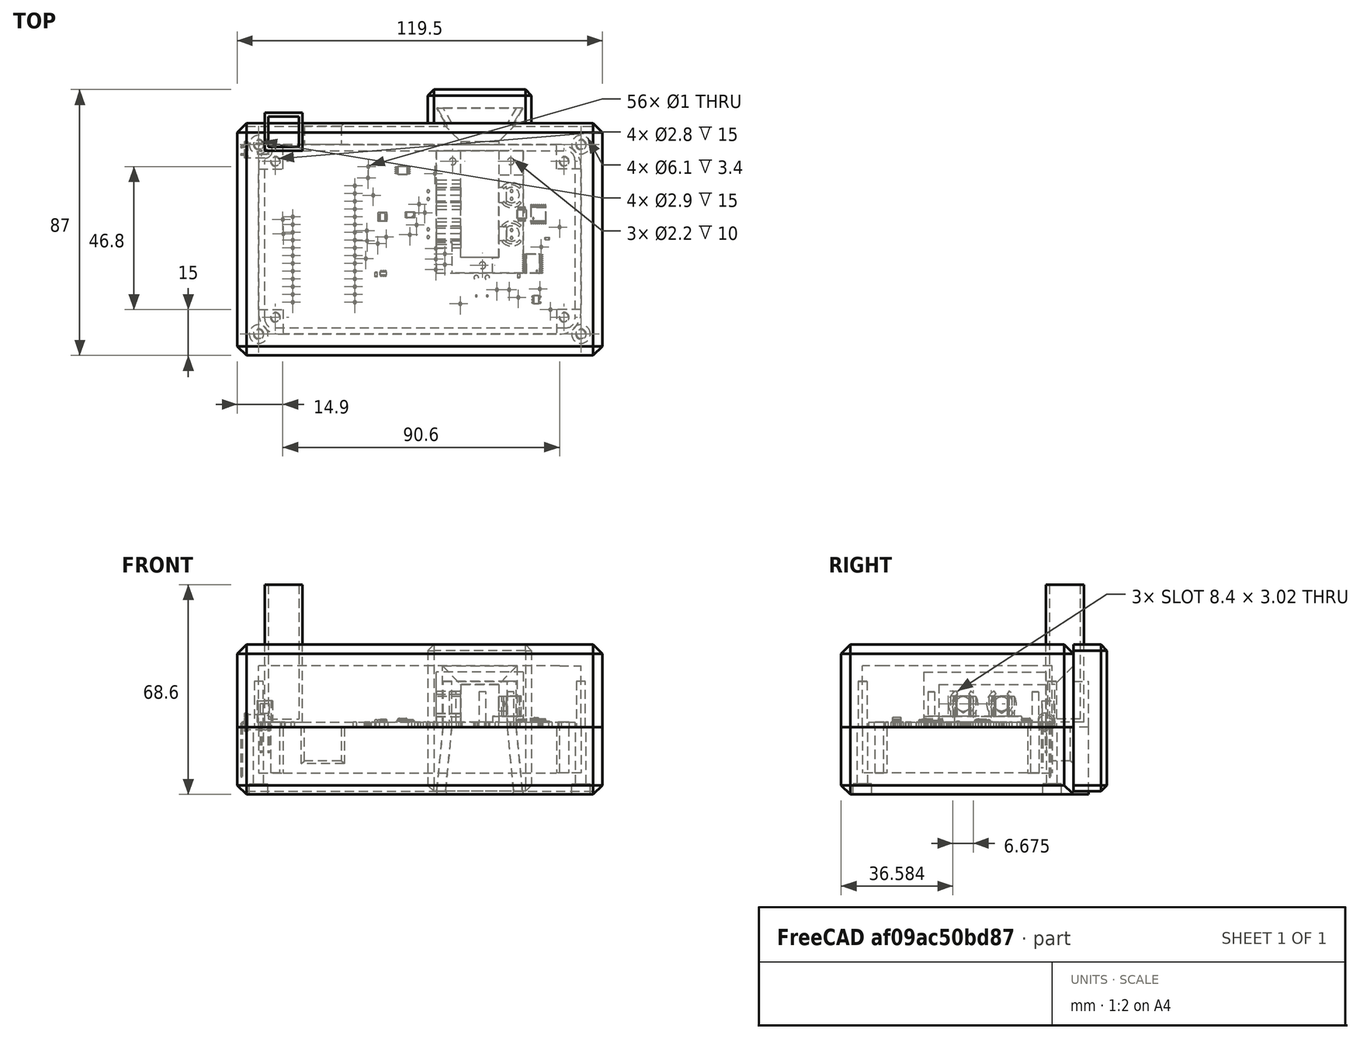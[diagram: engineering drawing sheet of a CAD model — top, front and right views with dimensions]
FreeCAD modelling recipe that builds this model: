
FCSTD DOCUMENT  (FreeCAD 1.0R38641 +678 (Git))
Label: phoenix-assembly
License: All rights reserved
LicenseURL: https://en.wikipedia.org/wiki/All_rights_reserved
objects: App::Link×42, Sketcher::SketchObject×42, PartDesign::SubShapeBinder×18, App::FeaturePython×16, PartDesign::Pad×15, PartDesign::Pocket×15, App::Part×13, Part::Feature×12, PartDesign::Body×9, PartDesign::Chamfer×7, PartDesign::AdditivePipe×4, PartDesign::Revolution×2, PartDesign::Mirrored×2, Assembly::JointGroup×1, PartDesign::Plane×1, PartDesign::Hole×1, PartDesign::Fillet×1, PartDesign::SubtractiveLoft×1, Assembly::AssemblyObject×1
note: 266 computed .brp shape members not serialized (recipe doc carries the construction recipe); baked Part::Feature solids carry a one-line shape summary decoded from their .brp

FEATURE [App::Link] C12_C_0603_1608Metric_43dd25189e75_ln_  label="C5_C_0603_1608Metric_e1bb111b0e8a"
  LinkPlacement = pos=(49.8145,-5.55904,0) rot=(0,0,1;0rad)
  LinkedObject = -> Shape001
  Placement = pos=(49.8145,-5.55904,0) rot=(0,0,1;0rad)
FEATURE [App::Link] C12_C_0603_1608Metric_43dd25189e75_ln_001  label="C18_C_0603_1608Metric_cf3f1f72a176"
  LinkPlacement = pos=(95.875,-19.7599,0) rot=(0,0,1;3.14159rad)
  LinkedObject = -> Shape001
  Placement = pos=(95.875,-19.7599,0) rot=(0,0,1;3.14159rad)
FEATURE [App::Link] C12_C_0603_1608Metric_43dd25189e75_ln_002  label="C7_C_0603_1608Metric_5fe292424d0b"
  LinkPlacement = pos=(49.0629,-7.83495,0) rot=(0,0,-1;1.5708rad)
  LinkedObject = -> Shape001
  Placement = pos=(49.0629,-7.83495,0) rot=(0,0,-1;1.5708rad)
FEATURE [App::Link] C12_C_0603_1608Metric_43dd25189e75_ln_003  label="C6_C_0603_1608Metric_6f7ce299bd57"
  LinkPlacement = pos=(39.475,-8.325,0) rot=(0,0,-1;1.5708rad)
  LinkedObject = -> Shape001
  Placement = pos=(39.475,-8.325,0) rot=(0,0,-1;1.5708rad)
FEATURE [App::Link] C12_C_0603_1608Metric_43dd25189e75_ln_004  label="C13_C_0603_1608Metric_2d995ea0f250"
  LinkPlacement = pos=(81.6,-40.775,0) rot=(0,0,-1;1.5708rad)
  LinkedObject = -> Shape001
  Placement = pos=(81.6,-40.775,0) rot=(0,0,-1;1.5708rad)
FEATURE [App::Link] C12_C_0603_1608Metric_43dd25189e75_ln_005  label="C16_C_0603_1608Metric_2a5a0c6a626c"
  LinkPlacement = pos=(92.375,-41.2599,0) rot=(0,0,1;0rad)
  LinkedObject = -> Shape001
  Placement = pos=(92.375,-41.2599,0) rot=(0,0,1;0rad)
FEATURE [App::Link] C12_C_0603_1608Metric_43dd25189e75_ln_006  label="C9_C_0603_1608Metric_6faa5609496b"
  LinkPlacement = pos=(50.7242,-7.875,0) rot=(0,0,-1;1.5708rad)
  LinkedObject = -> Shape001
  Placement = pos=(50.7242,-7.875,0) rot=(0,0,-1;1.5708rad)
FEATURE [App::Link] C12_C_0603_1608Metric_43dd25189e75_ln_007  label="C11_C_0603_1608Metric_2912fba1d5fa"
  LinkPlacement = pos=(92,-48.2788,0) rot=(0,0,-1;1.5708rad)
  LinkedObject = -> Shape001
  Placement = pos=(92,-48.2788,0) rot=(0,0,-1;1.5708rad)
FEATURE [App::Link] C12_C_0603_1608Metric_43dd25189e75_ln_008  label="C2_C_0603_1608Metric_ffe2bc87c12a"
  LinkPlacement = pos=(45.1858,-3.83244,0) rot=(0,0,1;0rad)
  LinkedObject = -> Shape001
  Placement = pos=(45.1858,-3.83244,0) rot=(0,0,1;0rad)
FEATURE [App::Link] C12_C_0603_1608Metric_43dd25189e75_ln_009  label="C14_C_0603_1608Metric_45402db31f73"
  LinkPlacement = pos=(93.125,-38.3,0) rot=(0,0,1;0rad)
  LinkedObject = -> Shape001
  Placement = pos=(93.125,-38.3,0) rot=(0,0,1;0rad)
FEATURE [App::Link] C12_C_0603_1608Metric_43dd25189e75_ln_010  label="C15_C_0603_1608Metric_d5b246a7317c"
  LinkPlacement = pos=(92.825,-42.7599,0) rot=(0,0,1;0rad)
  LinkedObject = -> Shape001
  Placement = pos=(92.825,-42.7599,0) rot=(0,0,1;0rad)
FEATURE [App::Link] C12_C_0603_1608Metric_43dd25189e75_ln_011  label="C8_C_0603_1608Metric_9caa440274d4"
  LinkPlacement = pos=(40.7255,-37.7255,0) rot=(0,0,1;0rad)
  LinkedObject = -> Shape001
  Placement = pos=(40.7255,-37.7255,0) rot=(0,0,1;0rad)
FEATURE [App::Link] C12_C_0603_1608Metric_43dd25189e75_ln_012  label="C10_C_0603_1608Metric_0caffe4b230c"
  LinkPlacement = pos=(85.8,-48.3137,0) rot=(0,0,-1;1.5708rad)
  LinkedObject = -> Shape001
  Placement = pos=(85.8,-48.3137,0) rot=(0,0,-1;1.5708rad)
FEATURE [App::Link] C12_C_0603_1608Metric_43dd25189e75_ln_013  label="C3_C_0603_1608Metric_40e8dbfff7af"
  LinkPlacement = pos=(38.8755,-44.0755,0) rot=(0,0,1;0rad)
  LinkedObject = -> Shape001
  Placement = pos=(38.8755,-44.0755,0) rot=(0,0,1;0rad)
FEATURE [App::Link] C12_C_0603_1608Metric_43dd25189e75_ln_014  label="C1_C_0603_1608Metric_aabbb8dd865d"
  LinkPlacement = pos=(38.8255,-42.5755,0) rot=(0,0,1;0rad)
  LinkedObject = -> Shape001
  Placement = pos=(38.8255,-42.5755,0) rot=(0,0,1;0rad)
FEATURE [App::Link] C12_C_0603_1608Metric_43dd25189e75_ln_015  label="C17_C_0603_1608Metric_9f332281af99"
  LinkPlacement = pos=(90.675,-27.2599,0) rot=(0,0,1;3.14159rad)
  LinkedObject = -> Shape001
  Placement = pos=(90.675,-27.2599,0) rot=(0,0,1;3.14159rad)
FEATURE [App::Link] C12_C_0603_1608Metric_43dd25189e75_ln_016  label="C4_C_0603_1608Metric_842c1dc952ed"
  LinkPlacement = pos=(40.975,-8.325,0) rot=(0,0,-1;1.5708rad)
  LinkedObject = -> Shape001
  Placement = pos=(40.975,-8.325,0) rot=(0,0,-1;1.5708rad)
FEATURE [Sketcher::SketchObject] PCB_Sketch_bfa0
  ArcFitTolerance = 1e-06
  FullyConstrained = false
  MakeInternals = false
  sketch-geometry (8):
    g0: LineSegment StartX=3 StartY=0 StartZ=0 EndX=98.5 EndY=2.2e-15 EndZ=0
    g1: LineSegment StartX=101.5 StartY=-3 StartZ=0 EndX=101.5 EndY=-55 EndZ=0
    g2: LineSegment StartX=9e-16 StartY=-55 StartZ=0 EndX=-4e-16 EndY=-3 EndZ=0
    g3: LineSegment StartX=98.5 StartY=-58 StartZ=0 EndX=3 EndY=-58 EndZ=0
    g4: ArcOfCircle CenterX=98.5 CenterY=-55 CenterZ=0 NormalX=0 NormalY=0 NormalZ=-1 AngleXU=-3.14159 Radius=3 StartAngle=0 EndAngle=1.5708
    g5: ArcOfCircle CenterX=3 CenterY=-3 CenterZ=0 NormalX=0 NormalY=0 NormalZ=-1 AngleXU=3.90995e-07 Radius=3 StartAngle=0 EndAngle=1.5708
    g6: ArcOfCircle CenterX=3 CenterY=-55 CenterZ=0 NormalX=0 NormalY=0 NormalZ=-1 AngleXU=-1.5708 Radius=3 StartAngle=0 EndAngle=1.5708
    g7: ArcOfCircle CenterX=98.5 CenterY=-3 CenterZ=0 NormalX=0 NormalY=0 NormalZ=-1 AngleXU=1.5708 Radius=3 StartAngle=0 EndAngle=1.5708
  constraints (8):
    c: Coincident(g2,g6)
    c: Coincident(g2,g5)
    c: Coincident(g3,g6)
    c: Coincident(g0,g5)
    c: Coincident(g3,g4)
    c: Coincident(g0,g7)
    c: Coincident(g1,g4)
    c: Coincident(g1,g7)
FEATURE [App::Part] Board_Geoms_bfa0
  Group = -> [PCB_Sketch_bfa0]
  Origin = -> Origin003
FEATURE [Part::Feature] Pcb_bfa0
  Placement = pos=(-30,20,0) rot=(0,0,1;0rad)
  shape: bbox 101.5 x 58 x 1.6 mm, 85 faces (baked)
FEATURE [App::Link] R19_R_0603_1608Metric_e81c35781ce5_ln_  label="R7_R_0603_1608Metric_df876850ed1e"
  LinkPlacement = pos=(79.275,-40.2599,0) rot=(0,0,1;0rad)
  LinkedObject = -> Shape
  Placement = pos=(79.275,-40.2599,0) rot=(0,0,1;0rad)
FEATURE [App::Link] R19_R_0603_1608Metric_e81c35781ce5_ln_001  label="R2_R_0603_1608Metric_bdd129e940a4"
  LinkPlacement = pos=(50.675,-27,0) rot=(0,0,1;3.14159rad)
  LinkedObject = -> Shape
  Placement = pos=(50.675,-27,0) rot=(0,0,1;3.14159rad)
FEATURE [App::Link] R19_R_0603_1608Metric_e81c35781ce5_ln_002  label="Rset1_R_0603_1608Metric_0a43983b202c"
  LinkPlacement = pos=(42.825,-20.75,0) rot=(0,0,1;3.14159rad)
  LinkedObject = -> Shape
  Placement = pos=(42.825,-20.75,0) rot=(0,0,1;3.14159rad)
FEATURE [App::Link] R19_R_0603_1608Metric_e81c35781ce5_ln_003  label="R5_R_0603_1608Metric_04dba9f839b4"
  LinkPlacement = pos=(80.6,-22.2599,0) rot=(0,0,1;3.14159rad)
  LinkedObject = -> Shape
  Placement = pos=(80.6,-22.2599,0) rot=(0,0,1;3.14159rad)
FEATURE [App::Link] R19_R_0603_1608Metric_e81c35781ce5_ln_004  label="RFB2_R_0603_1608Metric_fa4530d1918e"
  LinkPlacement = pos=(85.575,-25.7,0) rot=(0,0,1;0rad)
  LinkedObject = -> Shape
  Placement = pos=(85.575,-25.7,0) rot=(0,0,1;0rad)
FEATURE [App::Link] R19_R_0603_1608Metric_e81c35781ce5_ln_005  label="R3_R_0603_1608Metric_ae32d66b5177"
  LinkPlacement = pos=(50.175,-13.5,0) rot=(0,0,1;3.14159rad)
  LinkedObject = -> Shape
  Placement = pos=(50.175,-13.5,0) rot=(0,0,1;3.14159rad)
FEATURE [App::Link] R19_R_0603_1608Metric_e81c35781ce5_ln_006  label="R8_R_0603_1608Metric_02c9f0a1c546"
  LinkPlacement = pos=(79.275,-38.7599,0) rot=(0,0,1;0rad)
  LinkedObject = -> Shape
  Placement = pos=(79.275,-38.7599,0) rot=(0,0,1;0rad)
FEATURE [App::Link] R19_R_0603_1608Metric_e81c35781ce5_ln_007  label="TH1_R_0603_1608Metric_4b5df4f6c50b"
  LinkPlacement = pos=(75.59,-48.925,0) rot=(0,0,-1;1.5708rad)
  LinkedObject = -> Shape
  Placement = pos=(75.59,-48.925,0) rot=(0,0,-1;1.5708rad)
FEATURE [App::Link] R19_R_0603_1608Metric_e81c35781ce5_ln_008  label="RFB1_R_0603_1608Metric_a867aa814863"
  LinkPlacement = pos=(86.1875,-15.9037,0) rot=(0,0,1;0rad)
  LinkedObject = -> Shape
  Placement = pos=(86.1875,-15.9037,0) rot=(0,0,1;0rad)
FEATURE [App::Link] R19_R_0603_1608Metric_e81c35781ce5_ln_009  label="R14_R_0603_1608Metric_45fedd258f38"
  LinkPlacement = pos=(78.99,-48.925,0) rot=(0,0,1;1.5708rad)
  LinkedObject = -> Shape
  Placement = pos=(78.99,-48.925,0) rot=(0,0,1;1.5708rad)
FEATURE [App::Link] R19_R_0603_1608Metric_e81c35781ce5_ln_010  label="R10_R_0603_1608Metric_8ec42b163691"
  LinkPlacement = pos=(79.275,-35.7599,0) rot=(0,0,1;0rad)
  LinkedObject = -> Shape
  Placement = pos=(79.275,-35.7599,0) rot=(0,0,1;0rad)
FEATURE [App::Link] R19_R_0603_1608Metric_e81c35781ce5_ln_011  label="R18_R_0603_1608Metric_ee66729e9e05"
  LinkPlacement = pos=(72.7879,-49.6484,0) rot=(0,0,1;3.14159rad)
  LinkedObject = -> Shape
  Placement = pos=(72.7879,-49.6484,0) rot=(0,0,1;3.14159rad)
FEATURE [App::Link] R19_R_0603_1608Metric_e81c35781ce5_ln_012  label="R11_R_0603_1608Metric_a362d15d1ace"
  LinkPlacement = pos=(79.275,-34.2599,0) rot=(0,0,1;0rad)
  LinkedObject = -> Shape
  Placement = pos=(79.275,-34.2599,0) rot=(0,0,1;0rad)
FEATURE [App::Link] R19_R_0603_1608Metric_e81c35781ce5_ln_013  label="R12_R_0603_1608Metric_e843cbb940e9"
  LinkPlacement = pos=(79.275,-32.7599,0) rot=(0,0,1;0rad)
  LinkedObject = -> Shape
  Placement = pos=(79.275,-32.7599,0) rot=(0,0,1;0rad)
FEATURE [App::Link] R19_R_0603_1608Metric_e81c35781ce5_ln_014  label="R20_R_0603_1608Metric_bd504c419ae9"
  LinkPlacement = pos=(95.775,-18.2599,0) rot=(0,0,1;3.14159rad)
  LinkedObject = -> Shape
  Placement = pos=(95.775,-18.2599,0) rot=(0,0,1;3.14159rad)
FEATURE [App::Link] R19_R_0603_1608Metric_e81c35781ce5_ln_015  label="R17_R_0603_1608Metric_f07c92bcc6ee"
  LinkPlacement = pos=(77.19,-48.925,0) rot=(0,0,1;1.5708rad)
  LinkedObject = -> Shape
  Placement = pos=(77.19,-48.925,0) rot=(0,0,1;1.5708rad)
FEATURE [App::Link] R19_R_0603_1608Metric_e81c35781ce5_ln_016  label="Rout1_R_0603_1608Metric_3044a5c279e2"
  LinkPlacement = pos=(42.825,-22.25,0) rot=(0,0,1;3.14159rad)
  LinkedObject = -> Shape
  Placement = pos=(42.825,-22.25,0) rot=(0,0,1;3.14159rad)
FEATURE [App::Link] R19_R_0603_1608Metric_e81c35781ce5_ln_017  label="R13_R_0603_1608Metric_49b6a3b2dfdc"
  LinkPlacement = pos=(79.275,-41.7599,0) rot=(0,0,1;0rad)
  LinkedObject = -> Shape
  Placement = pos=(79.275,-41.7599,0) rot=(0,0,1;0rad)
FEATURE [App::Link] R19_R_0603_1608Metric_e81c35781ce5_ln_018  label="R4_R_0603_1608Metric_bbc76c5892d3"
  LinkPlacement = pos=(80.4982,-18.4451,0) rot=(0,0,1;3.14159rad)
  LinkedObject = -> Shape
  Placement = pos=(80.4982,-18.4451,0) rot=(0,0,1;3.14159rad)
FEATURE [App::Link] R19_R_0603_1608Metric_e81c35781ce5_ln_019  label="R1_R_0603_1608Metric_013c2982079e"
  LinkPlacement = pos=(47.175,-18.25,0) rot=(0,0,1;3.14159rad)
  LinkedObject = -> Shape
  Placement = pos=(47.175,-18.25,0) rot=(0,0,1;3.14159rad)
FEATURE [App::Link] R19_R_0603_1608Metric_e81c35781ce5_ln_020  label="R15_R_0603_1608Metric_c2b8edb76dc4"
  LinkPlacement = pos=(80.5,-48.925,0) rot=(0,0,-1;1.5708rad)
  LinkedObject = -> Shape
  Placement = pos=(80.5,-48.925,0) rot=(0,0,-1;1.5708rad)
FEATURE [App::Link] R19_R_0603_1608Metric_e81c35781ce5_ln_021  label="R16_R_0603_1608Metric_54fdf4ed7c6a"
  LinkPlacement = pos=(89.775,-42.7599,0) rot=(0,0,1;0rad)
  LinkedObject = -> Shape
  Placement = pos=(89.775,-42.7599,0) rot=(0,0,1;0rad)
FEATURE [App::Link] R19_R_0603_1608Metric_e81c35781ce5_ln_022  label="R6_R_0603_1608Metric_41f89ef6f0c9"
  LinkPlacement = pos=(76.5,-39.5849,0) rot=(0,0,1;1.5708rad)
  LinkedObject = -> Shape
  Placement = pos=(76.5,-39.5849,0) rot=(0,0,1;1.5708rad)
FEATURE [App::Link] R19_R_0603_1608Metric_e81c35781ce5_ln_023  label="R9_R_0603_1608Metric_e9602802d778"
  LinkPlacement = pos=(79.275,-37.2599,0) rot=(0,0,1;0rad)
  LinkedObject = -> Shape
  Placement = pos=(79.275,-37.2599,0) rot=(0,0,1;0rad)
FEATURE [App::Link] R19_R_0603_1608Metric_e81c35781ce5_ln_024  label="FB1_R_0603_1608Metric_30314544b1ba"
  LinkPlacement = pos=(52.753,-6.075,0) rot=(0,0,1;1.5708rad)
  LinkedObject = -> Shape
  Placement = pos=(52.753,-6.075,0) rot=(0,0,1;1.5708rad)
FEATURE [Part::Feature] Shape  label="R19_R_0603_1608Metric_e81c35781ce5"
  Placement = pos=(92.475,-28.7599,0) rot=(0,0,1;0rad)
  shape: bbox 1.6 x 0.8 x 0.45 mm, 26 faces (baked)
FEATURE [Part::Feature] Shape001  label="C12_C_0603_1608Metric_43dd25189e75"
  Placement = pos=(83.1,-40.775,0) rot=(0,0,-1;1.5708rad)
  shape: bbox 0.8 x 1.6 x 0.8 mm, 28 faces (baked)
FEATURE [Part::Feature] Shape002  label="U1_VSSOP-8_3x3mm_P0.65mm_b0bd8732d9d8"
  Placement = pos=(45.0875,-6.425,0) rot=(0,0,1;0rad)
  shape: bbox 4.9 x 3 x 1.35 mm, 147 faces (baked)
FEATURE [Part::Feature] Shape003  label="U7_MSOP_8_3x3mm_P065mm_0b8d5e192aae"
  Placement = pos=(84.125,-20.7287,0) rot=(0,0,-1;1.5708rad)
  shape: bbox 3 x 4.9 x 0.95 mm, 156 faces (baked)
FEATURE [Part::Feature] Shape005  label="U2_DFN-8-1EP_3x3mm_Pitch0.5mm_9c5140f70b24"
  Placement = pos=(38.585,-21.655,0) rot=(0,0,1;3.14159rad)
  shape: bbox 3 x 2.98 x 0.77 mm, 62 faces (baked)
FEATURE [Part::Feature] Shape006  label="U5_VSSOP_8_23x2mm_P05mm_af9a6c2f9d9d"
  Placement = pos=(47.6,-21,0) rot=(0,0,1;3.14159rad)
  shape: bbox 3.1 x 2 x 0.85 mm, 156 faces (baked)
FEATURE [Part::Feature] Shape007  label="U9_TSSOP_20_44x65mm_P065mm_1748040f196b"
  Placement = pos=(87.7375,-36.9349,0) rot=(0,0,1;3.14159rad)
  shape: bbox 6.4 x 6.5 x 1.2 mm, 336 faces (baked)
FEATURE [Part::Feature] Shape008  label="L1_L_0603_1608Metric_6e4b57586c89"
  Placement = pos=(36.4505,-40.513,0) rot=(0,0,1;1.5708rad)
  shape: bbox 0.8 x 1.6 x 0.8 mm, 28 faces (baked)
FEATURE [Part::Feature] Shape009  label="U3_SOT_363_SC_70_6_2b77724525eb"
  Placement = pos=(38.8005,-40.1255,0) rot=(0,0,1;1.5708rad)
  shape: bbox 2 x 2 x 1.05 mm, 118 faces (baked)
FEATURE [Part::Feature] Shape011  label="U8_TSSOP_16_44x5mm_P065mm_5ce80917f075"
  Placement = pos=(89.5375,-20.7662,0) rot=(0,0,1;1.5708rad)
  shape: bbox 5 x 6.4 x 1.1 mm, 260 faces (baked)
FEATURE [Part::Feature] Shape012  label="U6_SOT_23_5_cae0d91c1014"
  Placement = pos=(88.87,-48.7637,0) rot=(0,0,1;0rad)
  shape: bbox 2.8 x 2.9 x 1.55 mm, 109 faces (baked)
FEATURE [App::Part] Top_bfa0
  Group = -> [Shape,R19_R_0603_1608Metric_e81c35781ce5_ln_,Shape001,C12_C_0603_1608Metric_43dd25189e75_ln_,Shape002,Shape003,C12_C_0603_1608Metric_43dd25189e75_ln_001,C12_C_0603_1608Metric_43dd25189e75_ln_002,C12_C_0603_1608Metric_43dd25189e75_ln_003,R19_R_0603_1608Metric_e81c35781ce5_ln_001,R19_R_0603_1608Metric_e81c35781ce5_ln_002,Shape005,C12_C_0603_1608Metric_43dd25189e75_ln_004,+40 more]
  Origin = -> Origin006
FEATURE [App::Part] Step_Models_bfa0
  Group = -> [Top_bfa0]
  Origin = -> Origin005
FEATURE [App::Part] Board_bfa0  label="phoenix-main-board001"
  Group = -> [Board_Geoms_bfa0,Step_Models_bfa0,Pcb_bfa0]
  Origin = -> Origin004
FEATURE [Sketcher::SketchObject] Sketch002
  ArcFitTolerance = 1e-06
  AttachmentSupport = -> [XY_Plane007]
  FullyConstrained = true
  MakeInternals = false
  MapMode = 5
  sketch-geometry (8):
    g0: LineSegment StartX=-2e-15 StartY=2.45 StartZ=0 EndX=-5.55 EndY=2.45 EndZ=0
    g1: LineSegment StartX=-5.55 StartY=2.45 StartZ=0 EndX=-5.55 EndY=3 EndZ=0
    g2: LineSegment StartX=-5.55 StartY=3 StartZ=0 EndX=-6.55 EndY=3 EndZ=0
    g3: LineSegment StartX=-6.55 StartY=3 StartZ=0 EndX=-6.55 EndY=0 EndZ=0
    g4: ArcOfCircle CenterX=0 CenterY=0 CenterZ=0 NormalX=0 NormalY=0 NormalZ=1 AngleXU=0 Radius=2.45 StartAngle=0 EndAngle=1.5708
    g5: LineSegment StartX=2.45 StartY=0 StartZ=0 EndX=-6.55 EndY=0 EndZ=0
    g6: GeomPoint X=0 Y=0 Z=0
    g7: LineSegment [constr] StartX=-5.55 StartY=2.45 StartZ=0 EndX=-5.55 EndY=0 EndZ=0
  constraints (22):
    c: PointOnObject(g0,g-2)
    c: Horizontal(g0)
    c: Coincident(g0,g1)
    c: Vertical(g1)
    c: Coincident(g1,g2)
    c: Horizontal(g2)
    c: Coincident(g2,g3)
    c: Vertical(g3)
    c: Coincident(g4,g-1)
    c: Coincident(g4,g0)
    c: Horizontal(g5)
    c: PointOnObject(g6,g5)
    c: Coincident(g6,g4)
    c: Coincident(g7,g0)
    c: Vertical(g7)
    c: DistanceX(g2,g2) = 1
    c: Coincident(g4,g5)
    c: PointOnObject(g7,g5)
    c: Coincident(g3,g5)
    c: DistanceX(g5,g5) = 9
    c: DistanceY(g3,g3) = 3
    c: DistanceY(g7,g7) = 2.45
FEATURE [PartDesign::Revolution] Revolution
  Angle = 360
  Angle2 = 60
  Axis = (1,0,0)
  Base = (0,0,0)
  Profile = -> Sketch002
  ReferenceAxis = -> X_Axis007
  Refine = true
  Reversed = true
  Suppressed = false
  Type = 0
FEATURE [Sketcher::SketchObject] Sketch003
  ArcFitTolerance = 1e-06
  AttachmentSupport = -> [Revolution]
  FullyConstrained = true
  MakeInternals = false
  MapMode = 5
  Placement = pos=(-6.55,0,0) rot=(0.57735,-0.57735,-0.57735;2.0944rad)
  sketch-geometry (9):
    g0: LineSegment StartX=-1.5 StartY=0.25 StartZ=0 EndX=-1.5 EndY=-0.25 EndZ=0
    g1: LineSegment StartX=-1.5 StartY=-0.25 StartZ=0 EndX=-1 EndY=-0.25 EndZ=0
    g2: LineSegment StartX=-1 StartY=-0.25 StartZ=0 EndX=-1 EndY=0.25 EndZ=0
    g3: LineSegment StartX=-1 StartY=0.25 StartZ=0 EndX=-1.5 EndY=0.25 EndZ=0
    g4: LineSegment StartX=1 StartY=0.25 StartZ=0 EndX=1 EndY=-0.25 EndZ=0
    g5: LineSegment StartX=1 StartY=-0.25 StartZ=0 EndX=1.5 EndY=-0.25 EndZ=0
    g6: LineSegment StartX=1.5 StartY=-0.25 StartZ=0 EndX=1.5 EndY=0.25 EndZ=0
    g7: LineSegment StartX=1.5 StartY=0.25 StartZ=0 EndX=1 EndY=0.25 EndZ=0
    g8: LineSegment [constr] StartX=-1 StartY=0.25 StartZ=0 EndX=1 EndY=0.25 EndZ=0
  constraints (25):
    c: Coincident(g0,g1)
    c: Coincident(g1,g2)
    c: Coincident(g2,g3)
    c: Coincident(g3,g0)
    c: Vertical(g0)
    c: Vertical(g2)
    c: Horizontal(g1)
    c: Horizontal(g3)
    c: Coincident(g4,g5)
    c: Coincident(g5,g6)
    c: Coincident(g6,g7)
    c: Coincident(g7,g4)
    c: Vertical(g4)
    c: Vertical(g6)
    c: Horizontal(g5)
    c: Horizontal(g7)
    c: DistanceX(g3,g3) = 0.5
    c: DistanceY(g0,g0) = 0.5
    c: Equal(g7,g3)
    c: Coincident(g8,g2)
    c: Coincident(g8,g4)
    c: Horizontal(g8)
    c: Equal(g4,g0)
    c: Symmetric(g2,g4,g-1)
    c: DistanceX(g8,g8) = 2
FEATURE [Sketcher::SketchObject] Sketch004
  ArcFitTolerance = 1e-06
  AttachmentSupport = -> [XZ_Plane007,Revolution]
  ExternalGeometry = -> [Revolution]
  FullyConstrained = true
  MakeInternals = false
  MapMode = 5
  Placement = pos=(0,0,0) rot=(1,0,0;1.5708rad)
  sketch-geometry (4):
    g0: LineSegment StartX=-6.55 StartY=-2e-16 StartZ=0 EndX=-6.65 EndY=-2e-16 EndZ=0
    g1: LineSegment StartX=-7.65 StartY=-1 StartZ=0 EndX=-7.65 EndY=-15 EndZ=0
    g2: ArcOfCircle CenterX=-6.65 CenterY=-1 CenterZ=0 NormalX=0 NormalY=0 NormalZ=1 AngleXU=0 Radius=1 StartAngle=1.5708 EndAngle=3.14159
    g3: GeomPoint [constr] X=-7.65 Y=0 Z=0
  constraints (10):
    c: Symmetric(g-3,g-3,g0)
    c: PointOnObject(g3,g-1)
    c: Vertical(g1)
    c: PointOnObject(g3,g0)
    c: PointOnObject(g3,g1)
    c: Tangent(g0,g2) = -1.5708
    c: Tangent(g1,g2) = -1.5708
    c: DistanceX(g0,g0) = 0.1
    c: DistanceX(g1,g0) = 1
    c: DistanceY(g1,g1) = 14
FEATURE [Sketcher::SketchObject] Sketch005
  ArcFitTolerance = 1e-06
  AttachmentSupport = -> [Revolution]
  ExternalGeometry = -> [Sketch003]
  FullyConstrained = true
  MakeInternals = false
  MapMode = 5
  Placement = pos=(-6.55,0,0) rot=(0.57735,-0.57735,-0.57735;2.0944rad)
  sketch-geometry (4):
    g0: LineSegment StartX=1 StartY=0.25 StartZ=0 EndX=1.5 EndY=0.25 EndZ=0
    g1: LineSegment StartX=1.5 StartY=-0.25 StartZ=0 EndX=1.5 EndY=0.25 EndZ=0
    g2: LineSegment StartX=1 StartY=0.25 StartZ=0 EndX=1 EndY=-0.25 EndZ=0
    g3: LineSegment StartX=1 StartY=-0.25 StartZ=0 EndX=1.5 EndY=-0.25 EndZ=0
  constraints (8):
    c: Coincident(g0,g-6)
    c: Coincident(g0,g-4)
    c: Coincident(g1,g-5)
    c: Coincident(g1,g0)
    c: Coincident(g2,g0)
    c: Coincident(g2,g-6)
    c: Coincident(g3,g2)
    c: Coincident(g3,g1)
FEATURE [PartDesign::AdditivePipe] AdditivePipe
  AuxilleryCurvelinear = true
  AuxillerySpineTangent = false
  BaseFeature = -> Revolution
  Binormal = (0,0,0)
  Mode = 0
  Profile = -> Sketch005
  Refine = true
  Spine = -> Sketch004
  SpineTangent = false
  Suppressed = false
  Transformation = 0
  Transition = 0
FEATURE [Sketcher::SketchObject] Sketch006
  ArcFitTolerance = 1e-06
  AttachmentSupport = -> [Revolution]
  ExternalGeometry = -> [Sketch003]
  FullyConstrained = true
  MakeInternals = false
  MapMode = 5
  Placement = pos=(-6.55,0,0) rot=(0.57735,-0.57735,-0.57735;2.0944rad)
  sketch-geometry (4):
    g0: LineSegment StartX=-1.5 StartY=0.25 StartZ=0 EndX=-1 EndY=0.25 EndZ=0
    g1: LineSegment StartX=-1 StartY=0.25 StartZ=0 EndX=-1 EndY=-0.25 EndZ=0
    g2: LineSegment StartX=-1 StartY=-0.25 StartZ=0 EndX=-1.5 EndY=-0.25 EndZ=0
    g3: LineSegment StartX=-1.5 StartY=-0.25 StartZ=0 EndX=-1.5 EndY=0.25 EndZ=0
  constraints (8):
    c: Coincident(g0,g-6)
    c: Coincident(g0,g-4)
    c: Coincident(g1,g0)
    c: Coincident(g1,g-5)
    c: Coincident(g2,g-5)
    c: Coincident(g2,g-6)
    c: Coincident(g3,g2)
    c: Coincident(g3,g0)
FEATURE [PartDesign::AdditivePipe] AdditivePipe001
  AuxilleryCurvelinear = true
  AuxillerySpineTangent = false
  BaseFeature = -> AdditivePipe
  Binormal = (0,0,0)
  Mode = 0
  Profile = -> Sketch006
  Refine = true
  Spine = -> Sketch004
  SpineTangent = false
  Suppressed = false
  Transformation = 0
  Transition = 0
FEATURE [PartDesign::Pad] Pad001
  BaseFeature = -> AdditivePipe001
  Direction = (0,0,-1)
  Length = 3
  Length2 = 10
  Profile = -> AdditivePipe001 [Face21]
  Refine = true
  Suppressed = false
  Type = 0
FEATURE [Sketcher::SketchObject] Sketch007
  ArcFitTolerance = 1e-06
  AttachmentSupport = -> [Pad001]
  ExternalGeometry = -> [Pad001]
  FullyConstrained = true
  MakeInternals = false
  MapMode = 5
  Placement = pos=(-5.55,0,0) rot=(0.57735,0.57735,0.57735;2.0944rad)
  sketch-geometry (3):
    g0: LineSegment StartX=-2.45 StartY=1.73133 StartZ=0 EndX=-2.45 EndY=-1.73133 EndZ=0
    g1: ArcOfCircle CenterX=-1.1943e-05 CenterY=5e-16 CenterZ=0 NormalX=0 NormalY=0 NormalZ=1 AngleXU=0 Radius=2.99999 StartAngle=2.52641 EndAngle=3.75678
    g2: GeomPoint X=-2.45 Y=2e-16 Z=0
  constraints (8):
    c: PointOnObject(g0,g-3)
    c: PointOnObject(g0,g-3)
    c: Vertical(g0)
    c: Coincident(g1,g0)
    c: Coincident(g1,g0)
    c: Symmetric(g0,g0,g2)
    c: PointOnObject(g2,g-4)
    c: Tangent(g1,g-3)
FEATURE [PartDesign::Pocket] Pocket
  BaseFeature = -> Pad001
  Direction = (-1,0,0)
  Length = 5
  Length2 = 5
  Profile = -> Sketch007
  ReferenceAxis = -> Sketch007 [N_Axis]
  Refine = true
  Suppressed = false
  Type = 0
FEATURE [PartDesign::Body] Body001
  AllowCompound = false
  Group = -> [Sketch002,Revolution,Sketch003,Sketch004,Sketch005,Sketch006,AdditivePipe,AdditivePipe001,Pad001,Sketch007,Pocket]
  Origin = -> Origin007
  Tip = -> Pocket
FEATURE [App::Part] Part  label="LED"
  Group = -> [Body001]
  Origin = -> Origin008
  Placement = pos=(61.1489,-14.5251,6) rot=(0,0,1;0.000916rad)
FEATURE [Sketcher::SketchObject] Sketch008
  ArcFitTolerance = 1e-06
  AttachmentSupport = -> [XY_Plane009]
  FullyConstrained = true
  MakeInternals = false
  MapMode = 5
  sketch-geometry (8):
    g0: LineSegment StartX=-2e-15 StartY=2.45 StartZ=0 EndX=-5.55 EndY=2.45 EndZ=0
    g1: LineSegment StartX=-5.55 StartY=2.45 StartZ=0 EndX=-5.55 EndY=3 EndZ=0
    g2: LineSegment StartX=-5.55 StartY=3 StartZ=0 EndX=-6.55 EndY=3 EndZ=0
    g3: LineSegment StartX=-6.55 StartY=3 StartZ=0 EndX=-6.55 EndY=0 EndZ=0
    g4: ArcOfCircle CenterX=0 CenterY=0 CenterZ=0 NormalX=0 NormalY=0 NormalZ=1 AngleXU=0 Radius=2.45 StartAngle=0 EndAngle=1.5708
    g5: LineSegment StartX=2.45 StartY=0 StartZ=0 EndX=-6.55 EndY=0 EndZ=0
    g6: GeomPoint X=0 Y=0 Z=0
    g7: LineSegment [constr] StartX=-5.55 StartY=2.45 StartZ=0 EndX=-5.55 EndY=0 EndZ=0
  constraints (22):
    c: PointOnObject(g0,g-2)
    c: Horizontal(g0)
    c: Coincident(g0,g1)
    c: Vertical(g1)
    c: Coincident(g1,g2)
    c: Horizontal(g2)
    c: Coincident(g2,g3)
    c: Vertical(g3)
    c: Coincident(g4,g-1)
    c: Coincident(g4,g0)
    c: Horizontal(g5)
    c: PointOnObject(g6,g5)
    c: Coincident(g6,g4)
    c: Coincident(g7,g0)
    c: Vertical(g7)
    c: DistanceX(g2,g2) = 1
    c: Coincident(g4,g5)
    c: PointOnObject(g7,g5)
    c: Coincident(g3,g5)
    c: DistanceX(g5,g5) = 9
    c: DistanceY(g3,g3) = 3
    c: DistanceY(g7,g7) = 2.45
FEATURE [PartDesign::Revolution] Revolution001
  Angle = 360
  Angle2 = 60
  Axis = (1,0,0)
  Base = (0,0,0)
  Profile = -> Sketch008
  ReferenceAxis = -> X_Axis009
  Refine = true
  Reversed = true
  Suppressed = false
  Type = 0
FEATURE [Sketcher::SketchObject] Sketch009
  ArcFitTolerance = 1e-06
  AttachmentSupport = -> [Revolution001]
  FullyConstrained = true
  MakeInternals = false
  MapMode = 5
  Placement = pos=(-6.55,0,0) rot=(0.57735,-0.57735,-0.57735;2.0944rad)
  sketch-geometry (9):
    g0: LineSegment StartX=-1.5 StartY=0.25 StartZ=0 EndX=-1.5 EndY=-0.25 EndZ=0
    g1: LineSegment StartX=-1.5 StartY=-0.25 StartZ=0 EndX=-1 EndY=-0.25 EndZ=0
    g2: LineSegment StartX=-1 StartY=-0.25 StartZ=0 EndX=-1 EndY=0.25 EndZ=0
    g3: LineSegment StartX=-1 StartY=0.25 StartZ=0 EndX=-1.5 EndY=0.25 EndZ=0
    g4: LineSegment StartX=1 StartY=0.25 StartZ=0 EndX=1 EndY=-0.25 EndZ=0
    g5: LineSegment StartX=1 StartY=-0.25 StartZ=0 EndX=1.5 EndY=-0.25 EndZ=0
    g6: LineSegment StartX=1.5 StartY=-0.25 StartZ=0 EndX=1.5 EndY=0.25 EndZ=0
    g7: LineSegment StartX=1.5 StartY=0.25 StartZ=0 EndX=1 EndY=0.25 EndZ=0
    g8: LineSegment [constr] StartX=-1 StartY=0.25 StartZ=0 EndX=1 EndY=0.25 EndZ=0
  constraints (25):
    c: Coincident(g0,g1)
    c: Coincident(g1,g2)
    c: Coincident(g2,g3)
    c: Coincident(g3,g0)
    c: Vertical(g0)
    c: Vertical(g2)
    c: Horizontal(g1)
    c: Horizontal(g3)
    c: Coincident(g4,g5)
    c: Coincident(g5,g6)
    c: Coincident(g6,g7)
    c: Coincident(g7,g4)
    c: Vertical(g4)
    c: Vertical(g6)
    c: Horizontal(g5)
    c: Horizontal(g7)
    c: DistanceX(g3,g3) = 0.5
    c: DistanceY(g0,g0) = 0.5
    c: Equal(g7,g3)
    c: Coincident(g8,g2)
    c: Coincident(g8,g4)
    c: Horizontal(g8)
    c: Equal(g4,g0)
    c: Symmetric(g2,g4,g-1)
    c: DistanceX(g8,g8) = 2
FEATURE [Sketcher::SketchObject] Sketch010
  ArcFitTolerance = 1e-06
  AttachmentSupport = -> [XZ_Plane009,Revolution001]
  ExternalGeometry = -> [Revolution001]
  FullyConstrained = true
  MakeInternals = false
  MapMode = 5
  Placement = pos=(0,0,0) rot=(1,0,0;1.5708rad)
  sketch-geometry (4):
    g0: LineSegment StartX=-6.55 StartY=-2e-16 StartZ=0 EndX=-6.65 EndY=-2e-16 EndZ=0
    g1: LineSegment StartX=-7.65 StartY=-1 StartZ=0 EndX=-7.65 EndY=-15 EndZ=0
    g2: ArcOfCircle CenterX=-6.65 CenterY=-1 CenterZ=0 NormalX=0 NormalY=0 NormalZ=1 AngleXU=0 Radius=1 StartAngle=1.5708 EndAngle=3.14159
    g3: GeomPoint [constr] X=-7.65 Y=0 Z=0
  constraints (10):
    c: Symmetric(g-3,g-3,g0)
    c: PointOnObject(g3,g-1)
    c: Vertical(g1)
    c: PointOnObject(g3,g0)
    c: PointOnObject(g3,g1)
    c: Tangent(g0,g2) = -1.5708
    c: Tangent(g1,g2) = -1.5708
    c: DistanceX(g0,g0) = 0.1
    c: DistanceX(g1,g0) = 1
    c: DistanceY(g1,g1) = 14
FEATURE [Sketcher::SketchObject] Sketch011
  ArcFitTolerance = 1e-06
  AttachmentSupport = -> [Revolution001]
  ExternalGeometry = -> [Sketch009]
  FullyConstrained = true
  MakeInternals = false
  MapMode = 5
  Placement = pos=(-6.55,0,0) rot=(0.57735,-0.57735,-0.57735;2.0944rad)
  sketch-geometry (4):
    g0: LineSegment StartX=1 StartY=0.25 StartZ=0 EndX=1.5 EndY=0.25 EndZ=0
    g1: LineSegment StartX=1.5 StartY=-0.25 StartZ=0 EndX=1.5 EndY=0.25 EndZ=0
    g2: LineSegment StartX=1 StartY=0.25 StartZ=0 EndX=1 EndY=-0.25 EndZ=0
    g3: LineSegment StartX=1 StartY=-0.25 StartZ=0 EndX=1.5 EndY=-0.25 EndZ=0
  constraints (8):
    c: Coincident(g0,g-6)
    c: Coincident(g0,g-4)
    c: Coincident(g1,g-5)
    c: Coincident(g1,g0)
    c: Coincident(g2,g0)
    c: Coincident(g2,g-6)
    c: Coincident(g3,g2)
    c: Coincident(g3,g1)
FEATURE [PartDesign::AdditivePipe] AdditivePipe002
  AuxilleryCurvelinear = true
  AuxillerySpineTangent = false
  BaseFeature = -> Revolution001
  Binormal = (0,0,0)
  Mode = 0
  Profile = -> Sketch011
  Refine = true
  Spine = -> Sketch010
  SpineTangent = false
  Suppressed = false
  Transformation = 0
  Transition = 0
FEATURE [Sketcher::SketchObject] Sketch012
  ArcFitTolerance = 1e-06
  AttachmentSupport = -> [Revolution001]
  ExternalGeometry = -> [Sketch009]
  FullyConstrained = true
  MakeInternals = false
  MapMode = 5
  Placement = pos=(-6.55,0,0) rot=(0.57735,-0.57735,-0.57735;2.0944rad)
  sketch-geometry (4):
    g0: LineSegment StartX=-1.5 StartY=0.25 StartZ=0 EndX=-1 EndY=0.25 EndZ=0
    g1: LineSegment StartX=-1 StartY=0.25 StartZ=0 EndX=-1 EndY=-0.25 EndZ=0
    g2: LineSegment StartX=-1 StartY=-0.25 StartZ=0 EndX=-1.5 EndY=-0.25 EndZ=0
    g3: LineSegment StartX=-1.5 StartY=-0.25 StartZ=0 EndX=-1.5 EndY=0.25 EndZ=0
  constraints (8):
    c: Coincident(g0,g-6)
    c: Coincident(g0,g-4)
    c: Coincident(g1,g0)
    c: Coincident(g1,g-5)
    c: Coincident(g2,g-5)
    c: Coincident(g2,g-6)
    c: Coincident(g3,g2)
    c: Coincident(g3,g0)
FEATURE [PartDesign::AdditivePipe] AdditivePipe003
  AuxilleryCurvelinear = true
  AuxillerySpineTangent = false
  BaseFeature = -> AdditivePipe002
  Binormal = (0,0,0)
  Mode = 0
  Profile = -> Sketch012
  Refine = true
  Spine = -> Sketch010
  SpineTangent = false
  Suppressed = false
  Transformation = 0
  Transition = 0
FEATURE [PartDesign::Pad] Pad002
  BaseFeature = -> AdditivePipe003
  Direction = (0,0,-1)
  Length = 3
  Length2 = 10
  Profile = -> AdditivePipe003 [Face21]
  Refine = true
  Suppressed = false
  Type = 0
FEATURE [Sketcher::SketchObject] Sketch013
  ArcFitTolerance = 1e-06
  AttachmentSupport = -> [Pad002]
  ExternalGeometry = -> [Pad002]
  FullyConstrained = true
  MakeInternals = false
  MapMode = 5
  Placement = pos=(-5.55,0,0) rot=(0.57735,0.57735,0.57735;2.0944rad)
  sketch-geometry (3):
    g0: LineSegment StartX=-2.45 StartY=1.73133 StartZ=0 EndX=-2.45 EndY=-1.73133 EndZ=0
    g1: ArcOfCircle CenterX=-1.1943e-05 CenterY=5e-16 CenterZ=0 NormalX=0 NormalY=0 NormalZ=1 AngleXU=0 Radius=2.99999 StartAngle=2.52641 EndAngle=3.75678
    g2: GeomPoint X=-2.45 Y=2e-16 Z=0
  constraints (8):
    c: PointOnObject(g0,g-3)
    c: PointOnObject(g0,g-3)
    c: Vertical(g0)
    c: Coincident(g1,g0)
    c: Coincident(g1,g0)
    c: Symmetric(g0,g0,g2)
    c: PointOnObject(g2,g-4)
    c: Tangent(g1,g-3)
FEATURE [PartDesign::Pocket] Pocket001
  BaseFeature = -> Pad002
  Direction = (-1,0,0)
  Length = 5
  Length2 = 5
  Profile = -> Sketch013
  ReferenceAxis = -> Sketch013 [N_Axis]
  Refine = true
  Suppressed = false
  Type = 0
FEATURE [PartDesign::Body] Body002
  AllowCompound = false
  Group = -> [Sketch008,Revolution001,Sketch009,Sketch010,Sketch011,Sketch012,AdditivePipe002,AdditivePipe003,Pad002,Sketch013,Pocket001]
  Origin = -> Origin009
  Tip = -> Pocket001
FEATURE [App::Part] Part006  label="LED001"
  Group = -> [Body002]
  Origin = -> Origin010
  Placement = pos=(61.1606,-27.0787,6) rot=(0,0,-1;0.00872rad)
FEATURE [Sketcher::SketchObject] Sketch014
  ArcFitTolerance = 1e-06
  AttachmentSupport = -> [XY_Plane011]
  FullyConstrained = true
  MakeInternals = false
  MapMode = 5
  sketch-geometry (2):
    g0: ArcOfCircle CenterX=0 CenterY=0 CenterZ=0 NormalX=0 NormalY=0 NormalZ=1 AngleXU=0 Radius=2.5 StartAngle=5.78253 EndAngle=9.92543
    g1: LineSegment StartX=-2.19317 StartY=-1.2 StartZ=0 EndX=2.19317 EndY=-1.2 EndZ=0
  constraints (6):
    c: Coincident(g0,g-1)
    c: Diameter(g0) = 5
    c: Horizontal(g1)
    c: Distance(g0,g1) = -1.3
    c: Coincident(g0,g1)
    c: Coincident(g0,g1)
FEATURE [PartDesign::Pad] Pad003
  Direction = (0,0,1)
  Length = 7
  Length2 = 10
  Profile = -> Sketch014
  ReferenceAxis = -> Sketch014 [N_Axis]
  Refine = true
  Suppressed = false
  Type = 0
FEATURE [Sketcher::SketchObject] Sketch015
  ArcFitTolerance = 1e-06
  AttachmentSupport = -> [Pad003]
  FullyConstrained = true
  MakeInternals = false
  MapMode = 5
  Placement = pos=(0,0,0) rot=(1,0,0;3.14159rad)
  sketch-geometry (10):
    g0: LineSegment StartX=-1.5 StartY=0.25 StartZ=0 EndX=-1.5 EndY=-0.25 EndZ=0
    g1: LineSegment StartX=-1.5 StartY=-0.25 StartZ=0 EndX=-1 EndY=-0.25 EndZ=0
    g2: LineSegment StartX=-1 StartY=-0.25 StartZ=0 EndX=-1 EndY=0.25 EndZ=0
    g3: LineSegment StartX=-1 StartY=0.25 StartZ=0 EndX=-1.5 EndY=0.25 EndZ=0
    g4: LineSegment StartX=1 StartY=0.25 StartZ=0 EndX=1 EndY=-0.25 EndZ=0
    g5: LineSegment StartX=1 StartY=-0.25 StartZ=0 EndX=1.5 EndY=-0.25 EndZ=0
    g6: LineSegment StartX=1.5 StartY=-0.25 StartZ=0 EndX=1.5 EndY=0.25 EndZ=0
    g7: LineSegment StartX=1.5 StartY=0.25 StartZ=0 EndX=1 EndY=0.25 EndZ=0
    g8: GeomPoint X=-1 Y=0 Z=0
    g9: GeomPoint X=1 Y=0 Z=0
  constraints (25):
    c: Coincident(g0,g1)
    c: Coincident(g1,g2)
    c: Coincident(g2,g3)
    c: Coincident(g3,g0)
    c: Vertical(g0)
    c: Vertical(g2)
    c: Horizontal(g1)
    c: Horizontal(g3)
    c: Coincident(g4,g5)
    c: Coincident(g5,g6)
    c: Coincident(g6,g7)
    c: Coincident(g7,g4)
    c: Vertical(g4)
    c: Vertical(g6)
    c: Horizontal(g5)
    c: Horizontal(g7)
    c: Equal(g3,g2)
    c: Equal(g7,g6)
    c: Symmetric(g2,g2,g8)
    c: Symmetric(g4,g4,g9)
    c: Symmetric(g9,g8,g-1)
    c: PointOnObject(g9,g-1)
    c: DistanceX(g3,g3) = 0.5
    c: Equal(g3,g7)
    c: Distance(g4,g2) = 2
FEATURE [PartDesign::Pad] Pad004
  BaseFeature = -> Pad003
  Direction = (0,0,-1)
  Length = 10
  Length2 = 10
  Profile = -> Sketch015
  ReferenceAxis = -> Sketch015 [N_Axis]
  Refine = true
  Suppressed = false
  Type = 0
FEATURE [Sketcher::SketchObject] Sketch016
  ArcFitTolerance = 1e-06
  AttachmentSupport = -> [Pad004]
  ExternalGeometry = -> [Pad004]
  FullyConstrained = true
  MakeInternals = false
  MapMode = 5
  Placement = pos=(0,-1.2,0) rot=(1,0,0;1.5708rad)
  sketch-geometry (5):
    g0: LineSegment StartX=-1.5 StartY=6 StartZ=0 EndX=-1.5 EndY=3 EndZ=0
    g1: LineSegment StartX=-1.5 StartY=3 StartZ=0 EndX=1.5 EndY=3 EndZ=0
    g2: LineSegment StartX=1.5 StartY=3 StartZ=0 EndX=1.5 EndY=6 EndZ=0
    g3: LineSegment StartX=1.5 StartY=6 StartZ=0 EndX=-1.5 EndY=6 EndZ=0
    g4: GeomPoint X=0 Y=6 Z=0
  constraints (13):
    c: Coincident(g0,g1)
    c: Coincident(g1,g2)
    c: Coincident(g2,g3)
    c: Coincident(g3,g0)
    c: Vertical(g0)
    c: Vertical(g2)
    c: Horizontal(g1)
    c: Horizontal(g3)
    c: Symmetric(g3,g3,g4)
    c: PointOnObject(g4,g-2)
    c: DistanceX(g3,g3) = 3
    c: Equal(g2,g3)
    c: Distance(g-3,g3) = 1
FEATURE [PartDesign::Pocket] Pocket002
  BaseFeature = -> Pad004
  Direction = (0,1,-2e-16)
  Length = 0.1
  Length2 = 5
  Profile = -> Sketch016
  ReferenceAxis = -> Sketch016 [N_Axis]
  Refine = true
  Suppressed = false
  Type = 0
FEATURE [PartDesign::Body] Body003
  AllowCompound = false
  Group = -> [Sketch014,Pad003,Sketch015,Pad004,Sketch016,Pocket002]
  Origin = -> Origin011
  Tip = -> Pocket002
FEATURE [App::Part] Part007  label="Photodiode"
  Group = -> [Body003]
  Origin = -> Origin012
  Placement = pos=(80.806,-27.25,1.5) rot=(0,0,1;4.70367rad)
FEATURE [Sketcher::SketchObject] Sketch017
  ArcFitTolerance = 1e-06
  AttachmentSupport = -> [XY_Plane013]
  FullyConstrained = true
  MakeInternals = false
  MapMode = 5
  sketch-geometry (2):
    g0: ArcOfCircle CenterX=0 CenterY=0 CenterZ=0 NormalX=0 NormalY=0 NormalZ=1 AngleXU=0 Radius=2.5 StartAngle=5.78253 EndAngle=9.92543
    g1: LineSegment StartX=-2.19317 StartY=-1.2 StartZ=0 EndX=2.19317 EndY=-1.2 EndZ=0
  constraints (6):
    c: Coincident(g0,g-1)
    c: Diameter(g0) = 5
    c: Horizontal(g1)
    c: Distance(g0,g1) = -1.3
    c: Coincident(g0,g1)
    c: Coincident(g0,g1)
FEATURE [PartDesign::Pad] Pad005
  Direction = (0,0,1)
  Length = 7
  Length2 = 10
  Profile = -> Sketch017
  ReferenceAxis = -> Sketch017 [N_Axis]
  Refine = true
  Suppressed = false
  Type = 0
FEATURE [Sketcher::SketchObject] Sketch018
  ArcFitTolerance = 1e-06
  AttachmentSupport = -> [Pad005]
  FullyConstrained = true
  MakeInternals = false
  MapMode = 5
  Placement = pos=(0,0,0) rot=(1,0,0;3.14159rad)
  sketch-geometry (10):
    g0: LineSegment StartX=-1.5 StartY=0.25 StartZ=0 EndX=-1.5 EndY=-0.25 EndZ=0
    g1: LineSegment StartX=-1.5 StartY=-0.25 StartZ=0 EndX=-1 EndY=-0.25 EndZ=0
    g2: LineSegment StartX=-1 StartY=-0.25 StartZ=0 EndX=-1 EndY=0.25 EndZ=0
    g3: LineSegment StartX=-1 StartY=0.25 StartZ=0 EndX=-1.5 EndY=0.25 EndZ=0
    g4: LineSegment StartX=1 StartY=0.25 StartZ=0 EndX=1 EndY=-0.25 EndZ=0
    g5: LineSegment StartX=1 StartY=-0.25 StartZ=0 EndX=1.5 EndY=-0.25 EndZ=0
    g6: LineSegment StartX=1.5 StartY=-0.25 StartZ=0 EndX=1.5 EndY=0.25 EndZ=0
    g7: LineSegment StartX=1.5 StartY=0.25 StartZ=0 EndX=1 EndY=0.25 EndZ=0
    g8: GeomPoint X=-1 Y=0 Z=0
    g9: GeomPoint X=1 Y=0 Z=0
  constraints (25):
    c: Coincident(g0,g1)
    c: Coincident(g1,g2)
    c: Coincident(g2,g3)
    c: Coincident(g3,g0)
    c: Vertical(g0)
    c: Vertical(g2)
    c: Horizontal(g1)
    c: Horizontal(g3)
    c: Coincident(g4,g5)
    c: Coincident(g5,g6)
    c: Coincident(g6,g7)
    c: Coincident(g7,g4)
    c: Vertical(g4)
    c: Vertical(g6)
    c: Horizontal(g5)
    c: Horizontal(g7)
    c: Equal(g3,g2)
    c: Equal(g7,g6)
    c: Symmetric(g2,g2,g8)
    c: Symmetric(g4,g4,g9)
    c: Symmetric(g9,g8,g-1)
    c: PointOnObject(g9,g-1)
    c: DistanceX(g3,g3) = 0.5
    c: Equal(g3,g7)
    c: Distance(g4,g2) = 2
FEATURE [PartDesign::Pad] Pad006
  BaseFeature = -> Pad005
  Direction = (0,0,-1)
  Length = 10
  Length2 = 10
  Profile = -> Sketch018
  ReferenceAxis = -> Sketch018 [N_Axis]
  Refine = true
  Suppressed = false
  Type = 0
FEATURE [Sketcher::SketchObject] Sketch019
  ArcFitTolerance = 1e-06
  AttachmentSupport = -> [Pad006]
  ExternalGeometry = -> [Pad006]
  FullyConstrained = true
  MakeInternals = false
  MapMode = 5
  Placement = pos=(0,-1.2,0) rot=(1,0,0;1.5708rad)
  sketch-geometry (5):
    g0: LineSegment StartX=-1.5 StartY=6 StartZ=0 EndX=-1.5 EndY=3 EndZ=0
    g1: LineSegment StartX=-1.5 StartY=3 StartZ=0 EndX=1.5 EndY=3 EndZ=0
    g2: LineSegment StartX=1.5 StartY=3 StartZ=0 EndX=1.5 EndY=6 EndZ=0
    g3: LineSegment StartX=1.5 StartY=6 StartZ=0 EndX=-1.5 EndY=6 EndZ=0
    g4: GeomPoint X=0 Y=6 Z=0
  constraints (13):
    c: Coincident(g0,g1)
    c: Coincident(g1,g2)
    c: Coincident(g2,g3)
    c: Coincident(g3,g0)
    c: Vertical(g0)
    c: Vertical(g2)
    c: Horizontal(g1)
    c: Horizontal(g3)
    c: Symmetric(g3,g3,g4)
    c: PointOnObject(g4,g-2)
    c: DistanceX(g3,g3) = 3
    c: Equal(g2,g3)
    c: Distance(g-3,g3) = 1
FEATURE [PartDesign::Pocket] Pocket003
  BaseFeature = -> Pad006
  Direction = (0,1,-2e-16)
  Length = 0.1
  Length2 = 5
  Profile = -> Sketch019
  ReferenceAxis = -> Sketch019 [N_Axis]
  Refine = true
  Suppressed = false
  Type = 0
FEATURE [PartDesign::Body] Body004
  AllowCompound = false
  Group = -> [Sketch017,Pad005,Sketch018,Pad006,Sketch019,Pocket003]
  Origin = -> Origin013
  Tip = -> Pocket003
FEATURE [App::Part] Part008  label="Photodiode001"
  Group = -> [Body004]
  Origin = -> Origin014
  Placement = pos=(80.7939,-14.5071,1.5) rot=(0,0,-1;1.56988rad)
FEATURE [App::FeaturePython] GroundedJoint  # Assembly grounded joint (typed FeaturePython)
  ObjectToGround = -> Board_bfa0
FEATURE [Sketcher::SketchObject] Sketch020
  ArcFitTolerance = 1e-06
  AttachmentSupport = -> [XY_Plane015]
  FullyConstrained = true
  MakeInternals = false
  MapMode = 5
  sketch-geometry (4):
    g0: LineSegment StartX=0 StartY=0 StartZ=0 EndX=12.4 EndY=0 EndZ=0
    g1: LineSegment StartX=12.4 StartY=0 StartZ=0 EndX=12.4 EndY=12.4 EndZ=0
    g2: LineSegment StartX=12.4 StartY=12.4 StartZ=0 EndX=0 EndY=12.4 EndZ=0
    g3: LineSegment StartX=0 StartY=12.4 StartZ=0 EndX=0 EndY=0 EndZ=0
  constraints (11):
    c: Coincident(g0,g1)
    c: Coincident(g1,g2)
    c: Coincident(g2,g3)
    c: Coincident(g3,g0)
    c: Horizontal(g0)
    c: Horizontal(g2)
    c: Vertical(g1)
    c: Vertical(g3)
    c: Coincident(g0,g-1)
    c: DistanceX(g2,g2) = 12.4
    c: DistanceY(g3,g3) = 12.4
FEATURE [PartDesign::Pad] Pad007
  Direction = (0,0,1)
  Length = 45
  Length2 = 10
  Profile = -> Sketch020
  ReferenceAxis = -> Sketch020 [N_Axis]
  Refine = true
  Suppressed = false
  Type = 0
FEATURE [Sketcher::SketchObject] Sketch021
  ArcFitTolerance = 1e-06
  AttachmentSupport = -> [Pad007]
  ExternalGeometry = -> [Pad007]
  FullyConstrained = true
  MakeInternals = false
  MapMode = 5
  Placement = pos=(0,0,45) rot=(0,0,1;0rad)
  sketch-geometry (5):
    g0: LineSegment StartX=1.2 StartY=11.2 StartZ=0 EndX=1.2 EndY=1.2 EndZ=0
    g1: LineSegment StartX=1.2 StartY=1.2 StartZ=0 EndX=11.2 EndY=1.2 EndZ=0
    g2: LineSegment StartX=11.2 StartY=1.2 StartZ=0 EndX=11.2 EndY=11.2 EndZ=0
    g3: LineSegment StartX=11.2 StartY=11.2 StartZ=0 EndX=1.2 EndY=11.2 EndZ=0
    g4: GeomPoint X=6.2 Y=6.2 Z=0
  constraints (12):
    c: Coincident(g0,g1)
    c: Coincident(g1,g2)
    c: Coincident(g2,g3)
    c: Coincident(g3,g0)
    c: Vertical(g0)
    c: Vertical(g2)
    c: Horizontal(g1)
    c: Horizontal(g3)
    c: Symmetric(g0,g1,g4)
    c: Symmetric(g-3,g-1,g4)
    c: DistanceX(g3,g3) = 10
    c: DistanceY(g2,g2) = 10
FEATURE [App::FeaturePython] Joint  label="Cylindrical"  # Assembly joint (typed FeaturePython)
  Activated = true
  AngleMax = 0
  AngleMin = 0
  Detach1 = false
  Detach2 = false
  Distance = 0
  Distance2 = 0
  EnableAngleMax = false
  EnableAngleMin = false
  EnableLengthMax = false
  EnableLengthMin = false
  JointType = 2 (Cylindrical)
  LengthMax = 0
  LengthMin = 0
  Placement1 = pos=(-7.65,-1.25,-15) rot=(0,0,1;0rad)
  Placement2 = pos=(83.5,-48.262,-1.6) rot=(0,0,1;0rad)
  Reference1 = -> Assembly [Part006.Body002.Face16,Part006.Body002.Face16]
  Reference2 = -> Assembly [Board_bfa0.Board_Geoms_bfa0.Pcb_bfa0.Face53,Board_bfa0.Board_Geoms_bfa0.Pcb_bfa0.Edge3]
FEATURE [App::FeaturePython] Joint001  label="Cylindrical001"  # Assembly joint (typed FeaturePython)
  Activated = true
  AngleMax = 0
  AngleMin = 0
  Detach1 = false
  Detach2 = false
  Distance = 0
  Distance2 = 0
  EnableAngleMax = false
  EnableAngleMin = false
  EnableLengthMax = false
  EnableLengthMin = false
  JointType = 2 (Cylindrical)
  LengthMax = 0
  LengthMin = 0
  Placement1 = pos=(-7.65,-1.25,-15) rot=(0,0,1;0rad)
  Placement2 = pos=(83.5,-35.7821,-1.6) rot=(0,0,1;0rad)
  Reference1 = -> Assembly [Part.Body001.Face16,Part.Body001.Face16]
  Reference2 = -> Assembly [Board_bfa0.Board_Geoms_bfa0.Pcb_bfa0.Face56,Board_bfa0.Board_Geoms_bfa0.Pcb_bfa0.Edge3]
FEATURE [App::FeaturePython] Joint002  label="Parallel"  # Assembly joint (typed FeaturePython)
  Activated = true
  AngleMax = 0
  AngleMin = 0
  Detach1 = false
  Detach2 = false
  Distance = 0
  Distance2 = 0
  EnableAngleMax = false
  EnableAngleMin = false
  EnableLengthMax = false
  EnableLengthMin = false
  JointType = 6 (Parallel)
  LengthMax = 0
  LengthMin = 0
  Placement1 = pos=(-7.4,-1.5,-1) rot=(0.57735,0.57735,-0.57735;2.0944rad)
  Placement2 = pos=(80.75,-78,-0.8) rot=(0,0.707107,0.707107;3.14159rad)
  Reference1 = -> Assembly [Part006.Body002.Face9,Part006.Body002.Vertex30]
  Reference2 = -> Assembly [Board_bfa0.Board_Geoms_bfa0.Pcb_bfa0.Face8,Board_bfa0.Board_Geoms_bfa0.Pcb_bfa0.Face8]
FEATURE [App::FeaturePython] Joint003  label="Parallel001"  # Assembly joint (typed FeaturePython)
  Activated = true
  AngleMax = 0
  AngleMin = 0
  Detach1 = false
  Detach2 = false
  Distance = 0
  Distance2 = 0
  EnableAngleMax = false
  EnableAngleMin = false
  EnableLengthMax = false
  EnableLengthMin = false
  JointType = 6 (Parallel)
  LengthMax = 0
  LengthMin = 0
  Placement1 = pos=(-7.4,-1.5,-1) rot=(0.57735,0.57735,-0.57735;2.0944rad)
  Placement2 = pos=(80.75,-78,-0.8) rot=(0,0.707107,0.707107;3.14159rad)
  Reference1 = -> Assembly [Part.Body001.Face9,Part.Body001.Vertex30]
  Reference2 = -> Assembly [Board_bfa0.Board_Geoms_bfa0.Pcb_bfa0.Face8,Board_bfa0.Board_Geoms_bfa0.Pcb_bfa0.Face8]
FEATURE [App::FeaturePython] Joint004  label="Cylindrical002"  # Assembly joint (typed FeaturePython)
  Activated = true
  AngleMax = 0
  AngleMin = 0
  Detach1 = false
  Detach2 = false
  Distance = 0
  Distance2 = 0
  EnableAngleMax = false
  EnableAngleMin = false
  EnableLengthMax = false
  EnableLengthMin = false
  JointType = 2 (Cylindrical)
  LengthMax = 0
  LengthMin = 0
  Placement1 = pos=(1.25,0,-10) rot=(0,0,1;0rad)
  Placement2 = pos=(110.795,-48.5,-1.6) rot=(0,0,1;0rad)
  Reference1 = -> Assembly [Part007.Body003.Face19,Part007.Body003.Face19]
  Reference2 = -> Assembly [Board_bfa0.Board_Geoms_bfa0.Pcb_bfa0.Edge150,Board_bfa0.Board_Geoms_bfa0.Pcb_bfa0.Edge150]
FEATURE [App::FeaturePython] Joint005  label="Cylindrical003"  # Assembly joint (typed FeaturePython)
  Activated = true
  AngleMax = 0
  AngleMin = 0
  Detach1 = false
  Detach2 = false
  Distance = 0
  Distance2 = 0
  EnableAngleMax = false
  EnableAngleMin = false
  EnableLengthMax = false
  EnableLengthMin = false
  JointType = 2 (Cylindrical)
  LengthMax = 0
  LengthMin = 0
  Placement1 = pos=(1.25,0,-10) rot=(0,0,1;0rad)
  Placement2 = pos=(110.795,-35.7571,-1.6) rot=(0,0,1;0rad)
  Reference1 = -> Assembly [Part008.Body004.Face19,Part008.Body004.Face19]
  Reference2 = -> Assembly [Board_bfa0.Board_Geoms_bfa0.Pcb_bfa0.Face52,Board_bfa0.Board_Geoms_bfa0.Pcb_bfa0.Edge3]
FEATURE [App::FeaturePython] Joint006  label="Parallel002"  # Assembly joint (typed FeaturePython)
  Activated = true
  AngleMax = 0
  AngleMin = 0
  Detach1 = false
  Detach2 = false
  Distance = 0
  Distance2 = 0
  EnableAngleMax = false
  EnableAngleMin = false
  EnableLengthMax = false
  EnableLengthMin = false
  JointType = 6 (Parallel)
  LengthMax = 0
  LengthMin = 0
  Placement1 = pos=(1.5,0.25,0) rot=(-0.57735,0.57735,0.57735;4.18879rad)
  Placement2 = pos=(128.5,-78,-1.6) rot=(0,0.707107,0.707107;3.14159rad)
  Reference1 = -> Assembly [Part007.Body003.Face14,Part007.Body003.Vertex15]
  Reference2 = -> Assembly [Board_bfa0.Board_Geoms_bfa0.Pcb_bfa0.Face8,Board_bfa0.Board_Geoms_bfa0.Pcb_bfa0.Vertex16]
FEATURE [App::FeaturePython] Joint007  label="Parallel003"  # Assembly joint (typed FeaturePython)
  Activated = true
  AngleMax = 0
  AngleMin = 0
  Detach1 = false
  Detach2 = false
  Distance = 0
  Distance2 = 0
  EnableAngleMax = false
  EnableAngleMin = false
  EnableLengthMax = false
  EnableLengthMin = false
  JointType = 6 (Parallel)
  LengthMax = 0
  LengthMin = 0
  Placement1 = pos=(1.5,-0.25,0) rot=(-0.57735,0.57735,0.57735;4.18879rad)
  Placement2 = pos=(128.5,-78,-1.6) rot=(0,0.707107,0.707107;3.14159rad)
  Reference1 = -> Assembly [Part008.Body004.Face14,Part008.Body004.Vertex13]
  Reference2 = -> Assembly [Board_bfa0.Board_Geoms_bfa0.Pcb_bfa0.Face8,Board_bfa0.Board_Geoms_bfa0.Pcb_bfa0.Vertex16]
FEATURE [App::FeaturePython] Joint008  label="Distance"  # Assembly joint (typed FeaturePython)
  Activated = true
  AngleMax = 0
  AngleMin = 0
  Detach1 = false
  Detach2 = false
  Distance = 0
  Distance2 = 0
  EnableAngleMax = false
  EnableAngleMin = false
  EnableLengthMax = false
  EnableLengthMin = false
  JointType = 5 (Distance)
  LengthMax = 0
  LengthMin = 0
  Placement1 = pos=(0,0.451444,7) rot=(0,0,1;0rad)
  Placement2 = pos=(-1e-16,0.451444,7) rot=(0,0,1;0rad)
  Reference1 = -> Assembly [Part008.Body004.Face4,Part008.Body004.Face4]
  Reference2 = -> Assembly [Part007.Body003.Face4,Part007.Body003.Face4]
FEATURE [App::FeaturePython] Joint009  label="Cylindrical004"  # Assembly joint (typed FeaturePython)
  Activated = true
  AngleMax = 0
  AngleMin = 0
  Detach1 = false
  Detach2 = false
  Distance = 0
  Distance2 = 0
  EnableAngleMax = false
  EnableAngleMin = false
  EnableLengthMax = false
  EnableLengthMin = false
  JointType = 2 (Cylindrical)
  LengthMax = 0
  LengthMin = 0
  Placement1 = pos=(0,-1.1,4.5) rot=(0.57735,0.57735,0.57735;4.18879rad)
  Placement2 = pos=(-2e-15,0,0) rot=(-0.57735,-0.57735,0.57735;2.0944rad)
  Reference1 = -> Assembly [Part007.Body003.Face17,Part007.Body003.Face17]
  Reference2 = -> Assembly [Part006.Body002.Face1,Part006.Body002.Edge4]
FEATURE [App::FeaturePython] Joint010  label="Cylindrical005"  # Assembly joint (typed FeaturePython)
  Activated = true
  AngleMax = 0
  AngleMin = 0
  Detach1 = false
  Detach2 = false
  Distance = 0
  Distance2 = 0
  EnableAngleMax = false
  EnableAngleMin = false
  EnableLengthMax = false
  EnableLengthMin = false
  JointType = 2 (Cylindrical)
  LengthMax = 0
  LengthMin = 0
  Placement1 = pos=(-2.775,0,0) rot=(-0.57735,-0.57735,0.57735;2.0944rad)
  Placement2 = pos=(0,-1.1,4.5) rot=(0.57735,0.57735,0.57735;4.18879rad)
  Reference1 = -> Assembly [Part.Body001.Face1,Part.Body001.Face1]
  Reference2 = -> Assembly [Part008.Body004.Face17,Part008.Body004.Face17]
FEATURE [App::FeaturePython] Joint011  label="Distance001"  # Assembly joint (typed FeaturePython)
  Activated = true
  AngleMax = 0
  AngleMin = 0
  Detach1 = false
  Detach2 = false
  Distance = 0
  Distance2 = 0
  EnableAngleMax = false
  EnableAngleMin = false
  EnableLengthMax = false
  EnableLengthMin = false
  JointType = 5 (Distance)
  LengthMax = 0
  LengthMin = 0
  Placement1 = pos=(6.2,12.4,22.5) rot=(0,-0.707107,0.707107;3.14159rad)
  Placement2 = pos=(80.7833,-49.0071,0) rot=(0,1,0;3.14159rad)
  Reference1 = -> Assembly [Part009.Body005.Face6,Part009.Body005.Face6]
  Reference2 = -> Assembly [Board_bfa0.Board_Geoms_bfa0.Pcb_bfa0.Face84,Board_bfa0.Board_Geoms_bfa0.Pcb_bfa0.Edge23]
FEATURE [App::FeaturePython] Joint012  label="Distance002"  # Assembly joint (typed FeaturePython)
  Activated = true
  AngleMax = 0
  AngleMin = 0
  Detach1 = false
  Detach2 = false
  Distance = -3
  Distance2 = 0
  EnableAngleMax = false
  EnableAngleMin = false
  EnableLengthMax = false
  EnableLengthMin = false
  JointType = 5 (Distance)
  LengthMax = 0
  LengthMin = 0
  Placement1 = pos=(12.4,6.2,22.5) rot=(-0.57735,-0.57735,0.57735;2.0944rad)
  Placement2 = pos=(-1.3e-15,-1.2,3.08534) rot=(-1,0,0;1.5708rad)
  Reference1 = -> Assembly [Part009.Body005.Face3,Part009.Body005.Face3]
  Reference2 = -> Assembly [Part008.Body004.Face2,Part008.Body004.Vertex5]
FEATURE [App::FeaturePython] Joint013  label="Distance003"  # Assembly joint (typed FeaturePython)
  Activated = true
  AngleMax = 0
  AngleMin = 0
  Detach1 = false
  Detach2 = false
  Distance = -10
  Distance2 = 0
  EnableAngleMax = false
  EnableAngleMin = false
  EnableLengthMax = false
  EnableLengthMin = false
  JointType = 5 (Distance)
  LengthMax = 0
  LengthMin = 0
  Placement1 = pos=(80.75,-20,-0.8) rot=(1,0,0;1.5708rad)
  Placement2 = pos=(6.2,6.2,45) rot=(0,0,1;0rad)
  Reference1 = -> Assembly [Board_bfa0.Board_Geoms_bfa0.Pcb_bfa0.Face1,Board_bfa0.Board_Geoms_bfa0.Pcb_bfa0.Face1]
  Reference2 = -> Assembly [Part009.Body005.Face5,Part009.Body005.?Vertex12]
FEATURE [PartDesign::Pocket] Pocket004
  BaseFeature = -> Pad007
  Direction = (0,0,-1)
  Length = 44
  Length2 = 5
  Profile = -> Sketch021
  ReferenceAxis = -> Sketch021 [N_Axis]
  Refine = true
  Suppressed = false
  Type = 0
FEATURE [PartDesign::Body] Body005  label="cuvette"
  AllowCompound = false
  Group = -> [Sketch020,Pad007,Sketch021,Pocket004]
  Origin = -> Origin015
  Tip = -> Pocket004
FEATURE [App::Part] Part009  label="Cuvette"
  Group = -> [Body005]
  Origin = -> Origin016
  Placement = pos=(64.2127,-35.0057,12.4) rot=(1,0.000458,-0.000458;4.71239rad)
FEATURE [App::FeaturePython] Joint014  label="Distance004"  # Assembly joint (typed FeaturePython)
  Activated = true
  AngleMax = 0
  AngleMin = 0
  Detach1 = false
  Detach2 = false
  Distance = -8.5
  Distance2 = 0
  EnableAngleMax = false
  EnableAngleMin = false
  EnableLengthMax = false
  EnableLengthMin = false
  JointType = 5 (Distance)
  LengthMax = 0
  LengthMin = 0
  Placement1 = pos=(-1e-16,0.451444,7) rot=(0,0,1;0rad)
  Placement2 = pos=(80.7833,-49.0071,0) rot=(0,1,0;3.14159rad)
  Reference1 = -> Assembly [Part007.Body003.Face4,Part007.Body003.Face4]
  Reference2 = -> Assembly [Board_bfa0.Pcb_bfa0.Face84,Board_bfa0.Pcb_bfa0.Vertex99]
FEATURE [Assembly::JointGroup] Joints
  Group = -> [GroundedJoint,Joint,Joint001,Joint002,Joint003,Joint004,Joint005,Joint006,Joint007,Joint008,Joint009,Joint010,Joint011,Joint012,Joint013,Joint014]
FEATURE [PartDesign::SubShapeBinder] Binder  label="Cuvette001"
  BindCopyOnChange = 0
  BindMode = 0
  ClaimChildren = false
  Context = -> Assembly [Part010.Body.Binder.]
  Fuse = false
  MakeFace = true
  OffsetFill = false
  OffsetIntersection = false
  OffsetJoinType = 0
  OffsetOpenResult = false
  PartialLoad = false
  Refine = true
  Relative = true
  Support = -> [Part009[Body005.Pocket004.Face1]]
  _Version = 2
FEATURE [PartDesign::SubShapeBinder] Binder001  label="PCB"
  BindCopyOnChange = 0
  BindMode = 0
  ClaimChildren = false
  Context = -> Assembly [Part010.Body.Binder001.]
  Fuse = false
  MakeFace = true
  OffsetFill = false
  OffsetIntersection = false
  OffsetJoinType = 0
  OffsetOpenResult = false
  PartialLoad = false
  Refine = true
  Relative = true
  Support = -> [Board_bfa0[Pcb_bfa0.Face84]]
  _Version = 2
FEATURE [PartDesign::SubShapeBinder] Binder002  label="LED1"
  BindCopyOnChange = 0
  BindMode = 0
  ClaimChildren = false
  Context = -> Assembly [Part010.Body.Binder002.]
  Fuse = false
  MakeFace = true
  OffsetFill = false
  OffsetIntersection = false
  OffsetJoinType = 0
  OffsetOpenResult = false
  PartialLoad = false
  Refine = true
  Relative = true
  Support = -> [Part[Body001.Pocket.Edge4]]
  _Version = 2
FEATURE [PartDesign::SubShapeBinder] Binder003  label="LED2"
  BindCopyOnChange = 0
  BindMode = 0
  ClaimChildren = false
  Context = -> Assembly [Part010.Body.Binder003.]
  Fuse = false
  MakeFace = true
  OffsetFill = false
  OffsetIntersection = false
  OffsetJoinType = 0
  OffsetOpenResult = false
  PartialLoad = false
  Refine = true
  Relative = true
  Support = -> [Part006[Body002.Pocket001.Edge4]]
  _Version = 2
FEATURE [PartDesign::SubShapeBinder] Binder004
  BindCopyOnChange = 0
  BindMode = 0
  ClaimChildren = false
  Context = -> Assembly [Part010.Body.Binder004.]
  Fuse = false
  MakeFace = true
  OffsetFill = false
  OffsetIntersection = false
  OffsetJoinType = 0
  OffsetOpenResult = false
  PartialLoad = false
  Refine = true
  Relative = true
  Support = -> [Part008[Body004.Pocket003.Face2]]
  _Version = 2
FEATURE [Sketcher::SketchObject] Sketch
  ArcFitTolerance = 1e-06
  AttachmentSupport = -> [Binder]
  ExternalGeometry = -> [Binder]
  FullyConstrained = true
  MakeInternals = false
  MapMode = 5
  Placement = pos=(0,0,12.4) rot=(0,0,1;0rad)
  sketch-geometry (6):
    g0: LineSegment StartX=56.1806 StartY=-40.0057 StartZ=0 EndX=84.5806 EndY=-40.0057 EndZ=0
    g1: LineSegment StartX=84.5806 StartY=-40.0057 StartZ=0 EndX=84.5806 EndY=0 EndZ=0
    g2: LineSegment StartX=84.5806 StartY=0 StartZ=0 EndX=56.1806 EndY=0 EndZ=0
    g3: LineSegment StartX=56.1806 StartY=0 StartZ=0 EndX=56.1806 EndY=-40.0057 EndZ=0
    g4: GeomPoint X=76.5806 Y=0 Z=0
    g5: GeomPoint X=64.1806 Y=0 Z=0
  constraints (16):
    c: Coincident(g0,g1)
    c: Coincident(g1,g2)
    c: Coincident(g2,g3)
    c: Coincident(g3,g0)
    c: Horizontal(g0)
    c: Horizontal(g2)
    c: Vertical(g1)
    c: Vertical(g3)
    c: PointOnObject(g1,g-1)
    c: PointOnObject(g4,g-5)
    c: PointOnObject(g5,g2)
    c: PointOnObject(g4,g2)
    c: PointOnObject(g5,g-3)
    c: DistanceX(g4,g1) = 8
    c: Distance(g5,g2) = 8
    c: Distance(g-4,g0) = 5
FEATURE [PartDesign::Pad] Pad
  Direction = (0,0,1)
  Length = 4
  Length2 = 10
  Profile = -> Sketch
  ReferenceAxis = -> Sketch [N_Axis]
  Refine = true
  Suppressed = false
  Type = 0
FEATURE [Sketcher::SketchObject] Sketch022
  ArcFitTolerance = 1e-06
  AttachmentSupport = -> [Pad]
  ExternalGeometry = -> [Binder,Pad]
  FullyConstrained = false
  MakeInternals = false
  MapMode = 5
  Placement = pos=(0,0,12.4) rot=(1,0,0;3.14159rad)
  sketch-geometry (9):
    g0: LineSegment StartX=56.1806 StartY=40.0057 StartZ=0 EndX=56.1806 EndY=0 EndZ=0
    g1: LineSegment StartX=56.1806 StartY=0 StartZ=0 EndX=64.1806 EndY=0 EndZ=0
    g2: LineSegment StartX=84.5806 StartY=0 StartZ=0 EndX=84.5806 EndY=40.0057 EndZ=0
    g3: LineSegment StartX=84.5806 StartY=40.0057 StartZ=0 EndX=56.1806 EndY=40.0057 EndZ=0
    g4: LineSegment StartX=76.6127 StartY=34.9943 StartZ=0 EndX=64.1806 EndY=34.9943 EndZ=0
    g5: LineSegment StartX=64.1806 StartY=34.9943 StartZ=0 EndX=64.1806 EndY=0 EndZ=0
    g6: LineSegment StartX=76.5806 StartY=0 StartZ=0 EndX=76.6127 EndY=0 EndZ=0
    g7: LineSegment StartX=76.6127 StartY=0 StartZ=0 EndX=76.6127 EndY=34.9943 EndZ=0
    g8: LineSegment StartX=76.5806 StartY=0 StartZ=0 EndX=84.5806 EndY=0 EndZ=0
  constraints (22):
    c: Coincident(g0,g1)
    c: Coincident(g8,g2)
    c: Coincident(g2,g3)
    c: Coincident(g3,g0)
    c: Vertical(g0)
    c: Vertical(g2)
    c: Horizontal(g1)
    c: Horizontal(g3)
    c: Coincident(g0,g-7)
    c: Coincident(g8,g-9)
    c: Coincident(g4,g5)
    c: Coincident(g6,g7)
    c: Coincident(g7,g4)
    c: Horizontal(g4)
    c: Horizontal(g6)
    c: Vertical(g5)
    c: Vertical(g7)
    c: Coincident(g4,g-5)
    c: PointOnObject(g5,g-3)
    c: Coincident(g1,g5)
    c: PointOnObject(g8,g-4)
    c: PointOnObject(g6,g8)
FEATURE [PartDesign::Pad] Pad008
  BaseFeature = -> Pad
  Direction = (0,0,-1)
  Length = 10
  Length2 = 10
  Profile = -> Sketch022
  ReferenceAxis = -> Sketch022 [N_Axis]
  Refine = true
  Suppressed = false
  Type = 3
  UpToFace = -> Binder001 [Face1]
FEATURE [Sketcher::SketchObject] Sketch023
  ArcFitTolerance = 1e-06
  AttachmentSupport = -> [Pad008]
  ExternalGeometry = -> [Binder003]
  FullyConstrained = false
  MakeInternals = false
  MapMode = 5
  Placement = pos=(56.1806,0,0) rot=(0.57735,-0.57735,-0.57735;2.0944rad)
  sketch-geometry (19):
    g0: ArcOfCircle CenterX=27.0787 CenterY=6 CenterZ=0 NormalX=0 NormalY=0 NormalZ=1 AngleXU=0 Radius=2.45 StartAngle=5.32325 EndAngle=10.3847
    g1: LineSegment StartX=25.6735 StartY=3.99308 StartZ=0 EndX=27.0787 EndY=3.0091 EndZ=0
    g2: LineSegment StartX=27.0787 StartY=3.0091 StartZ=0 EndX=28.484 EndY=3.99308 EndZ=0
    g3: LineSegment [constr] StartX=25.6735 StartY=3.99308 StartZ=0 EndX=28.484 EndY=3.99308 EndZ=0
    g4: Circle [constr] CenterX=27.0787 CenterY=6 CenterZ=0 NormalX=0 NormalY=0 NormalZ=1 AngleXU=0 Radius=3.65
    g5: Circle [constr] CenterX=27.0787 CenterY=6 CenterZ=0 NormalX=0 NormalY=0 NormalZ=1 AngleXU=0 Radius=4.85
    g6: ArcOfCircle CenterX=27.0787 CenterY=6 CenterZ=0 NormalX=0 NormalY=0 NormalZ=1 AngleXU=0 Radius=3.65 StartAngle=5.23599 EndAngle=7.33038
    g7: ArcOfCircle CenterX=27.0787 CenterY=6 CenterZ=0 NormalX=0 NormalY=0 NormalZ=1 AngleXU=0 Radius=4.85 StartAngle=5.23599 EndAngle=7.33038
    g8: LineSegment [constr] StartX=27.0787 StartY=6 StartZ=0 EndX=29.5037 EndY=1.79978 EndZ=0
    g9: LineSegment [constr] StartX=27.0787 StartY=6 StartZ=0 EndX=24.6537 EndY=1.79978 EndZ=0
    g10: LineSegment [constr] StartX=27.0787 StartY=6 StartZ=0 EndX=27.0787 EndY=1.15 EndZ=0
    g11: LineSegment [constr] StartX=27.0787 StartY=6 StartZ=0 EndX=29.5037 EndY=10.2002 EndZ=0
    g12: LineSegment [constr] StartX=27.0787 StartY=6 StartZ=0 EndX=24.6537 EndY=10.2002 EndZ=0
    g13: LineSegment StartX=29.5037 StartY=1.79978 StartZ=0 EndX=28.9037 EndY=2.83901 EndZ=0
    g14: LineSegment StartX=29.5037 StartY=10.2002 StartZ=0 EndX=28.9037 EndY=9.16099 EndZ=0
    g15: LineSegment StartX=24.6537 StartY=10.2002 StartZ=0 EndX=25.2537 EndY=9.16099 EndZ=0
    g16: LineSegment StartX=24.6537 StartY=1.79978 StartZ=0 EndX=25.2537 EndY=2.83901 EndZ=0
    g17: ArcOfCircle CenterX=27.0787 CenterY=6 CenterZ=0 NormalX=0 NormalY=0 NormalZ=1 AngleXU=0 Radius=3.65 StartAngle=2.0944 EndAngle=4.18879
    g18: ArcOfCircle CenterX=27.0787 CenterY=6 CenterZ=0 NormalX=0 NormalY=0 NormalZ=1 AngleXU=0 Radius=4.85 StartAngle=2.0944 EndAngle=4.18879
  constraints (51):
    c: Coincident(g0,g-3)
    c: Coincident(g2,g1)
    c: Vertical(g1,g0)
    c: Coincident(g3,g1)
    c: Coincident(g3,g2)
    c: Angle(g1,g3) = 0.610865
    c: Tangent(g0,g1) = -1.5708
    c: Tangent(g0,g2) = -1.5708
    c: Radius(g0) = 2.45
    c: Coincident(g4,g0)
    c: Coincident(g5,g0)
    c: Distance(g0,g4) = 1.2
    c: Distance(g5,g4) = 1.2
    c: Coincident(g6,g0)
    c: Coincident(g7,g0)
    c: Equal(g4,g6)
    c: Equal(g7,g5)
    c: Coincident(g8,g0)
    c: Coincident(g9,g0)
    c: Coincident(g10,g0)
    c: Vertical(g10)
    c: Coincident(g11,g0)
    c: Coincident(g12,g0)
    c: PointOnObject(g12,g18)
    c: Angle(g9,g10) = 0.523599
    c: Angle(g10,g8) = 0.523599
    c: Angle(g12,g10) = 2.61799
    c: Angle(g10,g11) = 2.61799
    c: Coincident(g13,g8)
    c: Coincident(g14,g11)
    c: PointOnObject(g14,g6)
    c: Coincident(g15,g12)
    c: PointOnObject(g15,g17)
    c: Coincident(g16,g9)
    c: PointOnObject(g16,g17)
    c: PointOnObject(g16,g9)
    c: PointOnObject(g13,g8)
    c: PointOnObject(g14,g11)
    c: PointOnObject(g15,g12)
    c: Coincident(g7,g8)
    c: Coincident(g6,g13)
    c: Coincident(g18,g9)
    c: PointOnObject(g17,g9)
    c: Equal(g6,g17)
    c: PointOnObject(g6,g11)
    c: PointOnObject(g17,g15)
    c: Coincident(g6,g17)
    c: Equal(g7,g18)
    c: Coincident(g7,g11)
    c: PointOnObject(g18,g12)
    c: Coincident(g7,g18)
FEATURE [Sketcher::SketchObject] Sketch024
  ArcFitTolerance = 1e-06
  AttachmentSupport = -> [Pad008]
  ExternalGeometry = -> [Binder002,Binder003]
  FullyConstrained = true
  MakeInternals = false
  MapMode = 5
  Placement = pos=(56.1806,0,0) rot=(0.57735,-0.57735,-0.57735;2.0944rad)
  sketch-geometry (4):
    g0: LineSegment StartX=14.5251 StartY=6 StartZ=0 EndX=27.0787 EndY=6 EndZ=0
    g1: LineSegment StartX=20.8019 StartY=11 StartZ=0 EndX=20.8019 EndY=1 EndZ=0
    g2: GeomPoint [constr] X=20.8019 Y=6 Z=0
    g3: GeomPoint [constr] X=20.8019 Y=6 Z=0
  constraints (7):
    c: Coincident(g0,g-3)
    c: Coincident(g0,g-4)
    c: Vertical(g1)
    c: Symmetric(g0,g0,g2)
    c: Symmetric(g1,g1,g3)
    c: Coincident(g3,g2)
    c: DistanceY(g1,g1) = 10
FEATURE [PartDesign::Plane] DatumPlane
  AttachmentSupport = -> [Sketch024]
  Length = 124.385
  MapMode = 7
  Placement = pos=(56.1806,-20.8019,6) rot=(0,0.707107,0.707107;3.14159rad)
  ResizeMode = 0
  Width = 64.8041
FEATURE [PartDesign::Pocket] Pocket005  label="LED Hole"
  BaseFeature = -> Pad008
  Direction = (1,0,0)
  Length = 5
  Length2 = 5
  Profile = -> Sketch023
  ReferenceAxis = -> Sketch023 [N_Axis]
  Refine = true
  Suppressed = false
  Type = 2
FEATURE [PartDesign::Mirrored] Mirrored  label="LED Hole Mirror"
  BaseFeature = -> Pocket005
  MirrorPlane = -> DatumPlane
  Originals = -> [Pocket005]
  Refine = true
  Suppressed = false
  TransformMode = 0
FEATURE [PartDesign::SubShapeBinder] Binder007
  BindCopyOnChange = 0
  BindMode = 0
  ClaimChildren = false
  Context = -> Assembly [Part010.Body.Binder007.]
  Fuse = false
  MakeFace = true
  OffsetFill = false
  OffsetIntersection = false
  OffsetJoinType = 0
  OffsetOpenResult = false
  PartialLoad = false
  Refine = true
  Relative = true
  Support = -> [Part008[Body004.Pocket003.Face4]]
  _Version = 2
FEATURE [Sketcher::SketchObject] Sketch025
  ArcFitTolerance = 1e-06
  AttachmentSupport = -> [Mirrored]
  ExternalGeometry = -> [Binder007,Binder004]
  FullyConstrained = true
  MakeInternals = false
  MapMode = 5
  Placement = pos=(0,0,0) rot=(1,0,0;3.14159rad)
  sketch-geometry (17):
    g0: ArcOfCircle CenterX=80.7939 CenterY=14.5071 CenterZ=0 NormalX=0 NormalY=0 NormalZ=1 AngleXU=0 Radius=2.5 StartAngle=4.01697 EndAngle=8.54756
    g1: LineSegment StartX=79.1957 StartY=16.4295 StartZ=0 EndX=79.1922 EndY=12.5876 EndZ=0
    g2: Circle [constr] CenterX=80.7939 CenterY=14.5071 CenterZ=0 NormalX=0 NormalY=0 NormalZ=1 AngleXU=0 Radius=3.3
    g3: Circle [constr] CenterX=80.7939 CenterY=14.5071 CenterZ=0 NormalX=0 NormalY=0 NormalZ=1 AngleXU=0 Radius=4.1
    g4: ArcOfCircle CenterX=80.7939 CenterY=14.5071 CenterZ=0 NormalX=0 NormalY=0 NormalZ=1 AngleXU=0 Radius=3.3 StartAngle=3.83972 EndAngle=5.58505
    g5: ArcOfCircle CenterX=80.7939 CenterY=14.5071 CenterZ=0 NormalX=0 NormalY=0 NormalZ=1 AngleXU=0 Radius=4.1 StartAngle=3.83972 EndAngle=5.58505
    g6: LineSegment [constr] StartX=80.7939 StartY=14.5071 StartZ=0 EndX=76.6939 EndY=14.5071 EndZ=0
    g7: LineSegment [constr] StartX=80.7939 StartY=14.5071 StartZ=0 EndX=77.6531 EndY=17.1425 EndZ=0
    g8: LineSegment [constr] StartX=80.7939 StartY=14.5071 StartZ=0 EndX=83.9347 EndY=17.1425 EndZ=0
    g9: LineSegment [constr] StartX=80.7939 StartY=14.5071 StartZ=0 EndX=77.6531 EndY=11.8717 EndZ=0
    g10: LineSegment [constr] StartX=80.7939 StartY=14.5071 StartZ=0 EndX=83.9347 EndY=11.8717 EndZ=0
    g11: LineSegment StartX=77.6531 StartY=17.1425 StartZ=0 EndX=78.266 EndY=16.6283 EndZ=0
    g12: LineSegment StartX=83.9347 StartY=17.1425 StartZ=0 EndX=83.3219 EndY=16.6283 EndZ=0
    g13: LineSegment StartX=83.9347 StartY=11.8717 StartZ=0 EndX=83.3219 EndY=12.3859 EndZ=0
    g14: LineSegment StartX=77.6531 StartY=11.8717 StartZ=0 EndX=78.266 EndY=12.3859 EndZ=0
    g15: ArcOfCircle CenterX=80.7939 CenterY=14.5071 CenterZ=0 NormalX=0 NormalY=0 NormalZ=1 AngleXU=0 Radius=3.3 StartAngle=0.698132 EndAngle=2.44346
    g16: ArcOfCircle CenterX=80.7939 CenterY=14.5071 CenterZ=0 NormalX=0 NormalY=0 NormalZ=1 AngleXU=0 Radius=4.1 StartAngle=0.698132 EndAngle=2.44346
  constraints (49):
    c: Coincident(g0,g-3)
    c: Equal(g0,g-3)
    c: Parallel(g1,g-4)
    c: Distance(g1,g-4) = 0.4
    c: Coincident(g0,g1)
    c: Coincident(g0,g1)
    c: Coincident(g2,g0)
    c: Coincident(g3,g2)
    c: Coincident(g4,g2)
    c: Coincident(g5,g2)
    c: Distance(g0,g2) = 0.8
    c: Distance(g2,g3) = 0.8
    c: Coincident(g6,g0)
    c: Horizontal(g6)
    c: Coincident(g7,g0)
    c: Coincident(g8,g7)
    c: PointOnObject(g8,g16)
    c: Coincident(g9,g7)
    c: Coincident(g10,g7)
    c: Coincident(g11,g7)
    c: Coincident(g12,g8)
    c: PointOnObject(g12,g15)
    c: Coincident(g13,g10)
    c: PointOnObject(g13,g4)
    c: PointOnObject(g14,g4)
    c: Coincident(g14,g9)
    c: PointOnObject(g14,g9)
    c: PointOnObject(g13,g10)
    c: PointOnObject(g12,g8)
    c: PointOnObject(g11,g7)
    c: Angle(g7,g6) = 0.698132
    c: Angle(g6,g9) = 0.698132
    c: Angle(g8,g6) = 2.44346
    c: Angle(g6,g10) = 2.44346
    c: Coincident(g16,g7)
    c: Coincident(g15,g11)
    c: PointOnObject(g4,g9)
    c: Coincident(g5,g9)
    c: Equal(g4,g15)
    c: PointOnObject(g15,g8)
    c: Coincident(g4,g15)
    c: Equal(g5,g16)
    c: PointOnObject(g16,g8)
    c: Coincident(g5,g16)
    c: Coincident(g5,g10)
    c: PointOnObject(g4,g10)
    c: Equal(g16,g3)
    c: Equal(g15,g2)
    c: PointOnObject(g6,g3)
FEATURE [PartDesign::Pocket] Pocket006  label="PD Hole1"
  BaseFeature = -> Mirrored
  Direction = (0,0,1)
  Length = 0
  Length2 = 5
  Profile = -> Sketch025
  ReferenceAxis = -> Sketch025 [N_Axis]
  Refine = true
  Suppressed = false
  Type = 3
  UpToFace = -> Binder007 [Face1]
FEATURE [Sketcher::SketchObject] Sketch026
  ArcFitTolerance = 1e-06
  AttachmentSupport = -> [Pocket006]
  ExternalGeometry = -> [Binder004]
  FullyConstrained = true
  MakeInternals = false
  MapMode = 5
  Placement = pos=(76.6127,0,0) rot=(0.57735,-0.57735,-0.57735;2.0944rad)
  sketch-geometry (3):
    g0: LineSegment [constr] StartX=13.0082 StartY=7.5 StartZ=0 EndX=16.0082 EndY=4.5 EndZ=0
    g1: GeomPoint X=14.5082 Y=6 Z=0
    g2: Circle CenterX=14.5082 CenterY=6 CenterZ=0 NormalX=0 NormalY=0 NormalZ=1 AngleXU=0 Radius=2.37132
  constraints (5):
    c: Coincident(g0,g-5)
    c: Coincident(g0,g-6)
    c: Symmetric(g0,g0,g1)
    c: Coincident(g2,g1)
    c: Distance(g0,g2) = 0.25
FEATURE [PartDesign::Pocket] Pocket007  label="PD Hole2"
  BaseFeature = -> Pocket006
  Direction = (1,0,0)
  Length = 0
  Length2 = 5
  Profile = -> Sketch026
  ReferenceAxis = -> Sketch026 [N_Axis]
  Refine = true
  Suppressed = false
  Type = 3
  UpToFace = -> Pocket006 [Face34]
FEATURE [PartDesign::Mirrored] Mirrored001  label="PD Mirror"
  BaseFeature = -> Pocket007
  MirrorPlane = -> DatumPlane
  Originals = -> [Pocket006,Pocket007]
  Refine = true
  Suppressed = false
  TransformMode = 0
FEATURE [Sketcher::SketchObject] Sketch027
  ArcFitTolerance = 1e-06
  AttachmentSupport = -> [Mirrored001]
  ExternalGeometry = -> [Binder001]
  FullyConstrained = true
  MakeInternals = false
  MapMode = 5
  Placement = pos=(0,0,0) rot=(1,0,0;3.14159rad)
  sketch-geometry (3):
    g0: Circle CenterX=71.25 CenterY=37.5 CenterZ=0 NormalX=0 NormalY=0 NormalZ=1 AngleXU=0 Radius=1.1
    g1: Circle CenterX=80.5 CenterY=3.5 CenterZ=0 NormalX=0 NormalY=0 NormalZ=1 AngleXU=0 Radius=1.1
    g2: Circle CenterX=61.5 CenterY=3.5 CenterZ=0 NormalX=0 NormalY=0 NormalZ=1 AngleXU=0 Radius=1.1
  constraints (6):
    c: Coincident(g0,g-3)
    c: Equal(g0,g-3)
    c: Coincident(g1,g-5)
    c: Equal(g1,g-5)
    c: Coincident(g2,g-4)
    c: Equal(g2,g-4)
FEATURE [PartDesign::Pocket] Pocket008
  BaseFeature = -> Mirrored001
  Direction = (0,0,1)
  Length = 10
  Length2 = 5
  Profile = -> Sketch027
  ReferenceAxis = -> Sketch027 [N_Axis]
  Refine = true
  Suppressed = false
  Type = 0
FEATURE [Sketcher::SketchObject] Sketch028
  ArcFitTolerance = 1e-06
  AttachmentSupport = -> [Pocket008]
  ExternalGeometry = -> [Pocket008]
  FullyConstrained = true
  MakeInternals = false
  MapMode = 5
  Placement = pos=(84.5806,0,0) rot=(0.57735,0.57735,0.57735;2.0944rad)
  sketch-geometry (4):
    g0: LineSegment StartX=-40.0057 StartY=0 StartZ=0 EndX=-8.00566 EndY=0 EndZ=0
    g1: LineSegment StartX=-8.00566 StartY=0 StartZ=0 EndX=-8.00566 EndY=2 EndZ=0
    g2: LineSegment StartX=-8.00566 StartY=2 StartZ=0 EndX=-40.0057 EndY=2 EndZ=0
    g3: LineSegment StartX=-40.0057 StartY=2 StartZ=0 EndX=-40.0057 EndY=0 EndZ=0
  constraints (11):
    c: Coincident(g0,g1)
    c: Coincident(g1,g2)
    c: Coincident(g2,g3)
    c: Coincident(g3,g0)
    c: Horizontal(g0)
    c: Horizontal(g2)
    c: Vertical(g1)
    c: Vertical(g3)
    c: Coincident(g0,g-3)
    c: DistanceX(g2,g2) = 32
    c: DistanceY(g1,g1) = 2
FEATURE [PartDesign::Pocket] Pocket009
  BaseFeature = -> Pocket008
  Direction = (-1,0,0)
  Length = 10
  Length2 = 5
  Profile = -> Sketch028
  ReferenceAxis = -> Sketch028 [N_Axis]
  Refine = true
  Suppressed = false
  Type = 0
FEATURE [Sketcher::SketchObject] Sketch029
  ArcFitTolerance = 1e-06
  AttachmentSupport = -> [Pocket009]
  ExternalGeometry = -> [Pocket009]
  FullyConstrained = true
  MakeInternals = false
  MapMode = 5
  Placement = pos=(56.1806,0,0) rot=(0.57735,-0.57735,-0.57735;2.0944rad)
  sketch-geometry (4):
    g0: LineSegment StartX=40.0057 StartY=0 StartZ=0 EndX=40.0057 EndY=2 EndZ=0
    g1: LineSegment StartX=40.0057 StartY=2 StartZ=0 EndX=30.0057 EndY=2 EndZ=0
    g2: LineSegment StartX=30.0057 StartY=2 StartZ=0 EndX=30.0057 EndY=0 EndZ=0
    g3: LineSegment StartX=30.0057 StartY=0 StartZ=0 EndX=40.0057 EndY=0 EndZ=0
  constraints (11):
    c: Coincident(g0,g1)
    c: Coincident(g1,g2)
    c: Coincident(g2,g3)
    c: Coincident(g3,g0)
    c: Vertical(g0)
    c: Vertical(g2)
    c: Horizontal(g1)
    c: Horizontal(g3)
    c: Coincident(g0,g-3)
    c: DistanceX(g1,g1) = 10
    c: Distance(g2,g2) = 2
FEATURE [PartDesign::Pocket] Pocket010  label="ReliefSPI"
  BaseFeature = -> Pocket009
  Direction = (1,0,0)
  Length = 5
  Length2 = 5
  Profile = -> Sketch029
  ReferenceAxis = -> Sketch029 [N_Axis]
  Refine = true
  Suppressed = false
  Type = 0
FEATURE [PartDesign::Body] Body
  AllowCompound = false
  Group = -> [Binder,Binder001,Binder002,Binder003,Binder004,Binder007,Sketch,Pad,Sketch022,Pad008,Sketch023,Sketch024,DatumPlane,Pocket005,Mirrored,Sketch025,Pocket006,Sketch026,Pocket007,Mirrored001,Sketch027,Pocket008,Sketch028,Pocket009,Sketch029,Pocket010]
  Origin = -> Origin018
  Tip = -> Pocket010
FEATURE [App::Part] Part010  label="Shroud"
  Group = -> [Body]
  Origin = -> Origin017
FEATURE [PartDesign::SubShapeBinder] Binder008
  BindCopyOnChange = 0
  BindMode = 0
  ClaimChildren = false
  Context = -> Assembly [Part011.Body006.Binder008.]
  Fuse = false
  MakeFace = true
  OffsetFill = false
  OffsetIntersection = false
  OffsetJoinType = 0
  OffsetOpenResult = false
  PartialLoad = false
  Refine = true
  Relative = true
  Support = -> [Board_bfa0[Pcb_bfa0.Face85]]
  _Version = 2
FEATURE [PartDesign::SubShapeBinder] Binder009
  BindCopyOnChange = 0
  BindMode = 0
  ClaimChildren = false
  Context = -> Assembly [Part011.Body006.Binder009.]
  Fuse = false
  MakeFace = true
  OffsetFill = false
  OffsetIntersection = false
  OffsetJoinType = 0
  OffsetOpenResult = false
  PartialLoad = false
  Refine = true
  Relative = true
  Support = -> [Part009[Body005.Pocket004.Face6]]
  _Version = 2
FEATURE [PartDesign::SubShapeBinder] Binder010
  BindCopyOnChange = 0
  BindMode = 0
  ClaimChildren = false
  Context = -> Assembly [Part011.Body006.Binder010.]
  Fuse = false
  MakeFace = true
  OffsetFill = false
  OffsetIntersection = false
  OffsetJoinType = 0
  OffsetOpenResult = false
  PartialLoad = false
  Refine = true
  Relative = true
  Support = -> [Part009[Body005.Pocket004.Face2]]
  _Version = 2
FEATURE [PartDesign::SubShapeBinder] Binder011
  BindCopyOnChange = 0
  BindMode = 0
  ClaimChildren = false
  Context = -> Assembly [Part011.Body006.Binder011.]
  Fuse = false
  MakeFace = true
  OffsetFill = false
  OffsetIntersection = false
  OffsetJoinType = 0
  OffsetOpenResult = false
  PartialLoad = false
  Refine = true
  Relative = true
  Support = -> [Part009[Body005.Pocket004.Face3]]
  _Version = 2
FEATURE [Sketcher::SketchObject] Sketch030
  ArcFitTolerance = 1e-06
  AttachmentSupport = -> [Binder008]
  ExternalGeometry = -> [Binder008]
  FullyConstrained = false
  MakeInternals = false
  MapMode = 5
  Placement = pos=(0,0,-1.6) rot=(1,0,0;3.14159rad)
  sketch-geometry (28):
    g0: Circle CenterX=3.5 CenterY=54.5 CenterZ=0 NormalX=0 NormalY=0 NormalZ=1 AngleXU=0 Radius=1.4
    g1: Circle CenterX=98 CenterY=54.5 CenterZ=0 NormalX=0 NormalY=0 NormalZ=1 AngleXU=0 Radius=1.4
    g2: Circle CenterX=98 CenterY=3.5 CenterZ=0 NormalX=0 NormalY=0 NormalZ=1 AngleXU=0 Radius=1.4
    g3: Circle CenterX=3.5 CenterY=3.5 CenterZ=0 NormalX=0 NormalY=0 NormalZ=1 AngleXU=0 Radius=1.4
    g4: LineSegment StartX=-2 StartY=52 StartZ=0 EndX=-2 EndY=6 EndZ=0
    g5: LineSegment StartX=103.5 StartY=6 StartZ=0 EndX=103.5 EndY=52 EndZ=0
    g6: LineSegment StartX=95.5 StartY=60 StartZ=0 EndX=6 EndY=60 EndZ=0
    g7: LineSegment StartX=-2 StartY=52 StartZ=0 EndX=6 EndY=52 EndZ=0
    g8: LineSegment StartX=6 StartY=52 StartZ=0 EndX=6 EndY=60 EndZ=0
    g9: LineSegment StartX=-2 StartY=6 StartZ=0 EndX=6 EndY=6 EndZ=0
    g10: LineSegment StartX=6 StartY=6 StartZ=0 EndX=6 EndY=-2 EndZ=0
    g11: LineSegment StartX=103.5 StartY=6 StartZ=0 EndX=95.5 EndY=6 EndZ=0
    g12: LineSegment StartX=95.5 StartY=6 StartZ=0 EndX=95.5 EndY=-2 EndZ=0
    g13: LineSegment StartX=103.5 StartY=52 StartZ=0 EndX=95.5 EndY=52 EndZ=0
    g14: LineSegment StartX=95.5 StartY=52 StartZ=0 EndX=95.5 EndY=60 EndZ=0
    g15: LineSegment StartX=-9 StartY=67 StartZ=0 EndX=-9 EndY=-9 EndZ=0
    g16: LineSegment StartX=-9 StartY=-9 StartZ=0 EndX=110.5 EndY=-9 EndZ=0
    g17: LineSegment StartX=110.5 StartY=-9 StartZ=0 EndX=110.5 EndY=67 EndZ=0
    g18: LineSegment StartX=110.5 StartY=67 StartZ=0 EndX=-9 EndY=67 EndZ=0
    g19: LineSegment [constr] StartX=6 StartY=60 StartZ=0 EndX=-28.0014 EndY=60 EndZ=0
    g20: LineSegment [constr] StartX=-2 StartY=59.8868 StartZ=0 EndX=-2 EndY=52 EndZ=0
    g21: LineSegment [constr] StartX=6 StartY=-2 StartZ=0 EndX=-2 EndY=-2 EndZ=0
    g22: LineSegment [constr] StartX=-2 StartY=-2 StartZ=0 EndX=-2 EndY=6 EndZ=0
    g23: LineSegment [constr] StartX=95.5 StartY=60 StartZ=0 EndX=103.5 EndY=60 EndZ=0
    g24: LineSegment [constr] StartX=103.5 StartY=60 StartZ=0 EndX=103.5 EndY=52 EndZ=0
    g25: LineSegment [constr] StartX=103.5 StartY=6 StartZ=0 EndX=103.5 EndY=-1.97275 EndZ=0
    g26: LineSegment [constr] StartX=103.5 StartY=-1.97275 StartZ=0 EndX=95.5 EndY=-1.97275 EndZ=0
    g27: LineSegment StartX=6 StartY=-2 StartZ=0 EndX=95.5 EndY=-2 EndZ=0
  constraints (74):
    c: Coincident(g0,g-3)
    c: Coincident(g1,g-9)
    c: Coincident(g2,g-8)
    c: Coincident(g-10,g3)
    c: Equal(g0,g3)
    c: Equal(g3,g2)
    c: Equal(g2,g1)
    c: Diameter(g0) = 2.8
    c: Vertical(g4)
    c: Vertical(g5)
    c: Horizontal(g6)
    c: Horizontal(g7)
    c: Coincident(g8,g7)
    c: Vertical(g8)
    c: Horizontal(g9)
    c: Coincident(g13,g14)
    c: Vertical(g14)
    c: Horizontal(g11)
    c: Vertical(g12)
    c: Coincident(g12,g11)
    c: Coincident(g9,g10)
    c: Vertical(g10)
    c: Equal(g7,g8)
    c: Equal(g8,g14)
    c: Equal(g14,g13)
    c: Equal(g13,g11)
    c: Equal(g11,g12)
    c: Equal(g12,g9)
    c: Equal(g9,g10)
    c: Distance(g8,g8) = 8
    c: Horizontal(g13)
    c: Coincident(g15,g16)
    c: Coincident(g16,g17)
    c: Coincident(g17,g18)
    c: Coincident(g18,g15)
    c: Vertical(g15)
    c: Vertical(g17)
    c: Horizontal(g16)
    c: Horizontal(g18)
    c: Coincident(g6,g8)
    c: Coincident(g4,g7)
    c: Coincident(g19,g6)
    c: Horizontal(g19)
    c: Coincident(g20,g4)
    c: Vertical(g20)
    c: Coincident(g21,g10)
    c: Coincident(g22,g21)
    c: Coincident(g22,g9)
    c: Coincident(g4,g9)
    c: Coincident(g5,g11)
    c: Coincident(g5,g13)
    c: Coincident(g6,g14)
    c: Coincident(g23,g6)
    c: Horizontal(g23)
    c: Coincident(g24,g23)
    c: Coincident(g24,g5)
    c: Coincident(g25,g5)
    c: Vertical(g25)
    c: Horizontal(g26)
    c: Coincident(g25,g26)
    c: Vertical(g24)
    c: Vertical(g22)
    c: Horizontal(g21)
    c: Distance(g6,g-4) = 2
    c: Distance(g4,g-5) = 2
    c: Distance(g15,g4) = 7
    c: Distance(g18,g6) = 7
    c: Distance(g5,g-6) = 2
    c: Distance(g17,g5) = 7
    c: Coincident(g27,g10)
    c: Coincident(g27,g12)
    c: Horizontal(g27)
    c: Distance(g27,g-7) = 2
    c: Distance(g16,g27) = 7
FEATURE [PartDesign::Pad] Pad009
  Direction = (0,0,-1)
  Length = 15
  Length2 = 10
  Profile = -> Sketch030
  ReferenceAxis = -> Sketch030 [N_Axis]
  Refine = true
  Suppressed = false
  Type = 0
FEATURE [Sketcher::SketchObject] Sketch031
  ArcFitTolerance = 1e-06
  AttachmentSupport = -> [Pad009]
  ExternalGeometry = -> [Pad009]
  FullyConstrained = true
  MakeInternals = false
  MapMode = 5
  Placement = pos=(0,0,-16.6) rot=(1,0,0;3.14159rad)
  sketch-geometry (4):
    g0: LineSegment StartX=-9 StartY=67 StartZ=0 EndX=-9 EndY=-9 EndZ=0
    g1: LineSegment StartX=-9 StartY=-9 StartZ=0 EndX=110.5 EndY=-9 EndZ=0
    g2: LineSegment StartX=110.5 StartY=-9 StartZ=0 EndX=110.5 EndY=67 EndZ=0
    g3: LineSegment StartX=110.5 StartY=67 StartZ=0 EndX=-9 EndY=67 EndZ=0
  constraints (10):
    c: Coincident(g0,g1)
    c: Coincident(g1,g2)
    c: Coincident(g2,g3)
    c: Coincident(g3,g0)
    c: Vertical(g0)
    c: Vertical(g2)
    c: Horizontal(g1)
    c: Horizontal(g3)
    c: Coincident(g0,g-3)
    c: Coincident(g1,g-4)
FEATURE [PartDesign::Pad] Pad010
  BaseFeature = -> Pad009
  Direction = (0,0,-1)
  Length = 7
  Length2 = 10
  Profile = -> Sketch031
  ReferenceAxis = -> Sketch031 [N_Axis]
  Refine = true
  Suppressed = false
  Type = 0
FEATURE [Sketcher::SketchObject] Sketch032
  ArcFitTolerance = 1e-06
  AttachmentSupport = -> [Pad010]
  ExternalGeometry = -> [Pad010,Binder008]
  FullyConstrained = true
  MakeInternals = false
  MapMode = 5
  Placement = pos=(0,9,0) rot=(0,0.707107,0.707107;3.14159rad)
  sketch-geometry (4):
    g0: LineSegment StartX=-25 StartY=-1.6 StartZ=0 EndX=-25 EndY=-12.6 EndZ=0
    g1: LineSegment StartX=-25 StartY=-12.6 StartZ=0 EndX=-13 EndY=-12.6 EndZ=0
    g2: LineSegment StartX=-13 StartY=-12.6 StartZ=0 EndX=-13 EndY=-1.6 EndZ=0
    g3: LineSegment StartX=-13 StartY=-1.6 StartZ=0 EndX=-25 EndY=-1.6 EndZ=0
  constraints (12):
    c: Coincident(g0,g1)
    c: Coincident(g1,g2)
    c: Coincident(g2,g3)
    c: Coincident(g3,g0)
    c: Vertical(g0)
    c: Vertical(g2)
    c: Horizontal(g1)
    c: Horizontal(g3)
    c: DistanceX(g1,g1) = 12
    c: Distance(g1,g-4) = 11
    c: Distance(g-2,g2) = 13
    c: PointOnObject(g2,g-4)
FEATURE [PartDesign::Pocket] Pocket011
  BaseFeature = -> Pad010
  Direction = (0,-1,2e-16)
  Length = 5
  Length2 = 5
  Profile = -> Sketch032
  ReferenceAxis = -> Sketch032 [N_Axis]
  Refine = true
  Suppressed = false
  Type = 2
FEATURE [PartDesign::SubShapeBinder] Binder012
  BindCopyOnChange = 0
  BindMode = 0
  ClaimChildren = false
  Context = -> Assembly [Part012.Body007.Binder012.]
  Fuse = false
  MakeFace = true
  OffsetFill = false
  OffsetIntersection = false
  OffsetJoinType = 0
  OffsetOpenResult = false
  PartialLoad = false
  Refine = true
  Relative = true
  Support = -> [Part011[Body006.Pocket011.]]
  _Version = 2
FEATURE [PartDesign::SubShapeBinder] Binder013
  BindCopyOnChange = 0
  BindMode = 0
  ClaimChildren = false
  Context = -> Assembly [Part012.Body007.Binder013.]
  Fuse = false
  MakeFace = true
  OffsetFill = false
  OffsetIntersection = false
  OffsetJoinType = 0
  OffsetOpenResult = false
  PartialLoad = false
  Refine = true
  Relative = true
  Support = -> [Part009[Body005.Pocket004.Face1]]
  _Version = 2
FEATURE [PartDesign::SubShapeBinder] Binder014
  BindCopyOnChange = 0
  BindMode = 0
  ClaimChildren = false
  Context = -> Assembly [Part012.Body007.Binder014.]
  Fuse = false
  MakeFace = true
  OffsetFill = false
  OffsetIntersection = false
  OffsetJoinType = 0
  OffsetOpenResult = false
  PartialLoad = false
  Refine = true
  Relative = true
  Support = -> [Part009[Body005.Pocket004.Face2]]
  _Version = 2
FEATURE [PartDesign::SubShapeBinder] Binder015
  BindCopyOnChange = 0
  BindMode = 0
  ClaimChildren = false
  Context = -> Assembly [Part012.Body007.Binder015.]
  Fuse = false
  MakeFace = true
  OffsetFill = false
  OffsetIntersection = false
  OffsetJoinType = 0
  OffsetOpenResult = false
  PartialLoad = false
  Refine = true
  Relative = true
  Support = -> [Part009[Body005.Pocket004.Face3]]
  _Version = 2
FEATURE [Sketcher::SketchObject] Sketch033
  ArcFitTolerance = 1e-06
  AttachmentSupport = -> [Binder012]
  ExternalGeometry = -> [Binder012]
  FullyConstrained = true
  MakeInternals = false
  MapMode = 5
  Placement = pos=(0,0,-1.6) rot=(0,0,1;0rad)
  sketch-geometry (16):
    g0: LineSegment StartX=-9 StartY=9 StartZ=0 EndX=-9 EndY=-67 EndZ=0
    g1: LineSegment StartX=-9 StartY=-67 StartZ=0 EndX=110.5 EndY=-67 EndZ=0
    g2: LineSegment StartX=110.5 StartY=-67 StartZ=0 EndX=110.5 EndY=9 EndZ=0
    g3: LineSegment StartX=110.5 StartY=9 StartZ=0 EndX=-9 EndY=9 EndZ=0
    g4: LineSegment StartX=103.5 StartY=-60 StartZ=0 EndX=103.5 EndY=2 EndZ=0
    g5: LineSegment StartX=103.5 StartY=2 StartZ=0 EndX=-2 EndY=2 EndZ=0
    g6: LineSegment StartX=-2 StartY=2 StartZ=0 EndX=-2 EndY=-60 EndZ=0
    g7: LineSegment StartX=-2 StartY=-60 StartZ=0 EndX=103.5 EndY=-60 EndZ=0
    g8: LineSegment [constr] StartX=6 StartY=2 StartZ=0 EndX=-2 EndY=2 EndZ=0
    g9: LineSegment [constr] StartX=-2 StartY=-6 StartZ=0 EndX=-2 EndY=2 EndZ=0
    g10: LineSegment [constr] StartX=95.5 StartY=2 StartZ=0 EndX=103.5 EndY=2 EndZ=0
    g11: LineSegment [constr] StartX=103.5 StartY=2 StartZ=0 EndX=103.5 EndY=-6 EndZ=0
    g12: LineSegment [constr] StartX=103.5 StartY=-52 StartZ=0 EndX=103.5 EndY=-60 EndZ=0
    g13: LineSegment [constr] StartX=95.5 StartY=-60 StartZ=0 EndX=103.5 EndY=-60 EndZ=0
    g14: LineSegment [constr] StartX=-2 StartY=-52 StartZ=0 EndX=-2 EndY=-60 EndZ=0
    g15: LineSegment [constr] StartX=6 StartY=-60 StartZ=0 EndX=-2 EndY=-60 EndZ=0
  constraints (40):
    c: Coincident(g0,g1)
    c: Coincident(g1,g2)
    c: Coincident(g2,g3)
    c: Coincident(g3,g0)
    c: Vertical(g0)
    c: Vertical(g2)
    c: Horizontal(g1)
    c: Horizontal(g3)
    c: Coincident(g0,g-4)
    c: Coincident(g1,g-6)
    c: Coincident(g4,g5)
    c: Coincident(g5,g6)
    c: Coincident(g6,g7)
    c: Coincident(g7,g4)
    c: Vertical(g4)
    c: Vertical(g6)
    c: Horizontal(g5)
    c: Horizontal(g7)
    c: Coincident(g8,g-7)
    c: Horizontal(g8)
    c: Coincident(g9,g-8)
    c: Coincident(g9,g8)
    c: Vertical(g9)
    c: Coincident(g10,g-7)
    c: Horizontal(g10)
    c: Coincident(g11,g10)
    c: Coincident(g11,g-10)
    c: Vertical(g11)
    c: Coincident(g12,g-10)
    c: Vertical(g12)
    c: Coincident(g13,g-9)
    c: Coincident(g13,g12)
    c: Horizontal(g13)
    c: Coincident(g14,g-8)
    c: Vertical(g14)
    c: Coincident(g15,g-9)
    c: Coincident(g15,g14)
    c: Horizontal(g15)
    c: Coincident(g14,g6)
    c: Coincident(g4,g10)
FEATURE [PartDesign::Pad] Pad011
  Direction = (0,0,1)
  Length = 20
  Length2 = 10
  Profile = -> Sketch033
  ReferenceAxis = -> Sketch033 [N_Axis]
  Refine = true
  Suppressed = false
  Type = 0
FEATURE [Sketcher::SketchObject] Sketch034
  ArcFitTolerance = 1e-06
  AttachmentSupport = -> [Pad011]
  ExternalGeometry = -> [Pad011]
  FullyConstrained = true
  MakeInternals = false
  MapMode = 5
  Placement = pos=(0,0,18.4) rot=(0,0,1;0rad)
  sketch-geometry (4):
    g0: LineSegment StartX=-9 StartY=9 StartZ=0 EndX=-9 EndY=-67 EndZ=0
    g1: LineSegment StartX=-9 StartY=-67 StartZ=0 EndX=110.5 EndY=-67 EndZ=0
    g2: LineSegment StartX=110.5 StartY=-67 StartZ=0 EndX=110.5 EndY=9 EndZ=0
    g3: LineSegment StartX=110.5 StartY=9 StartZ=0 EndX=-9 EndY=9 EndZ=0
  constraints (10):
    c: Coincident(g0,g1)
    c: Coincident(g1,g2)
    c: Coincident(g2,g3)
    c: Coincident(g3,g0)
    c: Vertical(g0)
    c: Vertical(g2)
    c: Horizontal(g1)
    c: Horizontal(g3)
    c: Coincident(g0,g-3)
    c: Coincident(g1,g-4)
FEATURE [PartDesign::Pad] Pad012
  BaseFeature = -> Pad011
  Direction = (0,0,1)
  Length = 7
  Length2 = 10
  Profile = -> Sketch034
  ReferenceAxis = -> Sketch034 [N_Axis]
  Refine = true
  Suppressed = false
  Type = 0
FEATURE [Sketcher::SketchObject] Sketch035
  ArcFitTolerance = 1e-06
  AttachmentSupport = -> [Pad012]
  ExternalGeometry = -> [Binder013,Binder015,Binder014,Pad012]
  FullyConstrained = true
  MakeInternals = false
  MapMode = 5
  Placement = pos=(0,9,0) rot=(0,0.707107,0.707107;3.14159rad)
  sketch-geometry (4):
    g0: LineSegment StartX=-76.5715 StartY=12.4 StartZ=0 EndX=-76.5715 EndY=-1.6 EndZ=0
    g1: LineSegment StartX=-76.5715 StartY=-1.6 StartZ=0 EndX=-64.1715 EndY=-1.6 EndZ=0
    g2: LineSegment StartX=-64.1715 StartY=-1.6 StartZ=0 EndX=-64.1715 EndY=12.4 EndZ=0
    g3: LineSegment StartX=-64.1715 StartY=12.4 StartZ=0 EndX=-76.5715 EndY=12.4 EndZ=0
  constraints (11):
    c: Coincident(g0,g1)
    c: Coincident(g1,g2)
    c: Coincident(g2,g3)
    c: Coincident(g3,g0)
    c: Vertical(g0)
    c: Vertical(g2)
    c: Horizontal(g1)
    c: Horizontal(g3)
    c: Coincident(g0,g-4)
    c: PointOnObject(g1,g-6)
    c: PointOnObject(g-5,g2)
FEATURE [PartDesign::Pocket] Pocket012
  BaseFeature = -> Pad012
  Direction = (0,-1,2e-16)
  Length = 5
  Length2 = 5
  Profile = -> Sketch035
  ReferenceAxis = -> Sketch035 [N_Axis]
  Refine = true
  Suppressed = false
  Type = 2
FEATURE [PartDesign::Chamfer] Chamfer
  Angle = 45
  Base = -> Pocket012 [Edge17,Edge16,Edge18]
  BaseFeature = -> Pocket012
  ChamferType = 0
  FlipDirection = false
  Refine = true
  Size = 6
  Size2 = 1
  SupportTransform = false
  Suppressed = false
  UseAllEdges = false
FEATURE [Sketcher::SketchObject] Sketch036
  ArcFitTolerance = 1e-06
  AttachmentSupport = -> [Pocket011]
  ExternalGeometry = -> [Pocket011]
  FullyConstrained = false
  MakeInternals = false
  MapMode = 5
  Placement = pos=(0,0,-23.6) rot=(1,0,0;3.14159rad)
  sketch-geometry (17):
    g0: LineSegment [constr] StartX=6 StartY=60 StartZ=0 EndX=-2 EndY=60 EndZ=0
    g1: LineSegment [constr] StartX=-2 StartY=52 StartZ=0 EndX=-2 EndY=60 EndZ=0
    g2: LineSegment [constr] StartX=95.5 StartY=60 StartZ=0 EndX=103.5 EndY=60 EndZ=0
    g3: LineSegment [constr] StartX=103.5 StartY=52 StartZ=0 EndX=103.5 EndY=60 EndZ=0
    g4: LineSegment [constr] StartX=103.5 StartY=6 StartZ=0 EndX=103.5 EndY=-2 EndZ=0
    g5: LineSegment [constr] StartX=95.5 StartY=-2 StartZ=0 EndX=103.5 EndY=-2 EndZ=0
    g6: LineSegment [constr] StartX=25 StartY=-2 StartZ=0 EndX=-2 EndY=-2 EndZ=0
    g7: LineSegment [constr] StartX=-2 StartY=6 StartZ=0 EndX=-2 EndY=-2 EndZ=0
    g8: GeomPoint X=-2 Y=60 Z=0
    g9: LineSegment [constr] StartX=-2 StartY=60 StartZ=0 EndX=-2 EndY=-2 EndZ=0
    g10: LineSegment [constr] StartX=-2 StartY=-2 StartZ=0 EndX=103.5 EndY=-2 EndZ=0
    g11: LineSegment [constr] StartX=103.5 StartY=-2 StartZ=0 EndX=103.5 EndY=60 EndZ=0
    g12: LineSegment [constr] StartX=103.5 StartY=60 StartZ=0 EndX=-2 EndY=60 EndZ=0
    g13: Circle CenterX=-2 CenterY=60 CenterZ=0 NormalX=0 NormalY=0 NormalZ=1 AngleXU=0 Radius=1.73566
    g14: Circle CenterX=103.5 CenterY=60 CenterZ=0 NormalX=0 NormalY=0 NormalZ=1 AngleXU=0 Radius=2.15156
    g15: Circle CenterX=103.5 CenterY=-2 CenterZ=0 NormalX=0 NormalY=0 NormalZ=1 AngleXU=0 Radius=1.49444
    g16: Circle CenterX=-2 CenterY=-2 CenterZ=0 NormalX=0 NormalY=0 NormalZ=1 AngleXU=0 Radius=1.09035
  constraints (35):
    c: Coincident(g0,g-9)
    c: Horizontal(g0)
    c: Coincident(g1,g-10)
    c: Coincident(g1,g0)
    c: Vertical(g1)
    c: Coincident(g2,g-9)
    c: Horizontal(g2)
    c: Coincident(g3,g-8)
    c: Coincident(g3,g2)
    c: Vertical(g3)
    c: Coincident(g4,g-8)
    c: Vertical(g4)
    c: Coincident(g5,g-7)
    c: Coincident(g5,g4)
    c: Horizontal(g5)
    c: Coincident(g6,g-7)
    c: Horizontal(g6)
    c: Coincident(g7,g-10)
    c: Coincident(g7,g6)
    c: Vertical(g7)
    c: Coincident(g8,g0)
    c: Coincident(g9,g10)
    c: Coincident(g10,g11)
    c: Coincident(g11,g12)
    c: Coincident(g12,g9)
    c: Vertical(g9)
    c: Vertical(g11)
    c: Horizontal(g10)
    c: Horizontal(g12)
    c: Coincident(g13,g9)
    c: Coincident(g14,g11)
    c: Coincident(g15,g10)
    c: Coincident(g16,g9)
    c: Coincident(g0,g9)
    c: Coincident(g10,g4)
FEATURE [PartDesign::Hole] Hole
  BaseFeature = -> Pocket011
  CustomThreadClearance = 0
  Depth = 289.504
  DepthType = 1
  Diameter = 3.4
  DrillForDepth = false
  DrillPoint = 1
  DrillPointAngle = 118
  HoleCutCountersinkAngle = 90
  HoleCutCustomValues = false
  HoleCutDepth = 3.4
  HoleCutDiameter = 6.1
  HoleCutType = 1
  ModelThread = false
  Profile = -> Sketch036
  Refine = true
  Suppressed = false
  Tapered = false
  TaperedAngle = 90
  ThreadClass = 0
  ThreadDepth = 289.504
  ThreadDepthType = 0
  ThreadDirection = 0
  ThreadFit = 0
  ThreadSize = 9
  ThreadType = 1
  Threaded = false
  UseCustomThreadClearance = false
FEATURE [PartDesign::SubShapeBinder] Binder016
  BindCopyOnChange = 0
  BindMode = 0
  ClaimChildren = false
  Context = -> Assembly [Part012.Body007.Binder016.]
  Fuse = false
  MakeFace = true
  OffsetFill = false
  OffsetIntersection = false
  OffsetJoinType = 0
  OffsetOpenResult = false
  PartialLoad = false
  Refine = true
  Relative = true
  Support = -> [Part011[Body006.Hole.Face1]]
  _Version = 2
FEATURE [PartDesign::Fillet] Fillet
  Base = -> Chamfer [Edge33,Edge31,Edge35,Edge37]
  BaseFeature = -> Chamfer
  Radius = 7
  Refine = true
  SupportTransform = false
  Suppressed = false
  UseAllEdges = false
FEATURE [Sketcher::SketchObject] Sketch037
  ArcFitTolerance = 1e-06
  AttachmentSupport = -> [Fillet]
  ExternalGeometry = -> [Binder016]
  FullyConstrained = true
  MakeInternals = false
  MapMode = 5
  Placement = pos=(0,0,-1.6) rot=(1,0,0;3.14159rad)
  sketch-geometry (4):
    g0: Circle CenterX=-2 CenterY=60 CenterZ=0 NormalX=0 NormalY=0 NormalZ=1 AngleXU=0 Radius=1.45
    g1: Circle CenterX=103.5 CenterY=60 CenterZ=0 NormalX=0 NormalY=0 NormalZ=1 AngleXU=0 Radius=1.45
    g2: Circle CenterX=103.5 CenterY=-2 CenterZ=0 NormalX=0 NormalY=0 NormalZ=1 AngleXU=0 Radius=1.45
    g3: Circle CenterX=-2 CenterY=-2 CenterZ=0 NormalX=0 NormalY=0 NormalZ=1 AngleXU=0 Radius=1.45
  constraints (8):
    c: Coincident(g0,g-3)
    c: Coincident(g1,g-4)
    c: Coincident(g2,g-5)
    c: Coincident(g3,g-6)
    c: Equal(g3,g0)
    c: Equal(g0,g1)
    c: Equal(g1,g2)
    c: Diameter(g2) = 2.9
FEATURE [PartDesign::Pocket] Pocket013
  BaseFeature = -> Fillet
  Direction = (0,0,1)
  Length = 15
  Length2 = 5
  Profile = -> Sketch037
  ReferenceAxis = -> Sketch037 [N_Axis]
  Refine = true
  Suppressed = false
  Type = 0
FEATURE [Sketcher::SketchObject] Sketch038
  ArcFitTolerance = 1e-06
  AttachmentSupport = -> [Hole]
  ExternalGeometry = -> [Binder009,Hole]
  FullyConstrained = true
  MakeInternals = false
  MapMode = 5
  Placement = pos=(0,0,-1.6) rot=(0,0,1;0rad)
  sketch-geometry (4):
    g0: LineSegment StartX=81.5715 StartY=9 StartZ=0 EndX=59.1715 EndY=9 EndZ=0
    g1: LineSegment StartX=59.1715 StartY=9 StartZ=0 EndX=56.2847 EndY=14 EndZ=0
    g2: LineSegment StartX=56.2847 StartY=14 StartZ=0 EndX=84.4582 EndY=14 EndZ=0
    g3: LineSegment StartX=84.4582 StartY=14 StartZ=0 EndX=81.5715 EndY=9 EndZ=0
  constraints (12):
    c: PointOnObject(g0,g-4)
    c: PointOnObject(g0,g-4)
    c: Coincident(g1,g0)
    c: Horizontal(g2)
    c: Coincident(g3,g2)
    c: Coincident(g3,g0)
    c: DistanceX(g-3,g0) = 5
    c: DistanceX(g0,g-3) = 5
    c: Angle(g1,g-4) = 1.0472
    c: Angle(g-4,g3) = 1.0472
    c: Distance(g0,g2) = 5
    c: Coincident(g1,g2)
FEATURE [PartDesign::Pad] Pad013
  BaseFeature = -> Hole
  Direction = (0,0,1)
  Length = 10
  Length2 = 10
  Profile = -> Sketch038
  ReferenceAxis = -> Sketch038 [N_Axis]
  Refine = true
  Reversed = true
  Suppressed = false
  Type = 3
  UpToFace = -> Hole [Face28]
FEATURE [PartDesign::Chamfer] Chamfer001
  Angle = 5
  Base = -> Pad013 [Edge71,Edge65]
  BaseFeature = -> Pad013
  ChamferType = 2
  FlipDirection = false
  Refine = true
  Size = 21
  Size2 = 1
  SupportTransform = false
  Suppressed = false
  UseAllEdges = false
FEATURE [PartDesign::SubShapeBinder] Binder017
  BindCopyOnChange = 0
  BindMode = 0
  ClaimChildren = false
  Context = -> Assembly [Part013.Body008.Binder017.]
  Fuse = false
  MakeFace = true
  OffsetFill = false
  OffsetIntersection = false
  OffsetJoinType = 0
  OffsetOpenResult = false
  PartialLoad = false
  Refine = true
  Relative = true
  Support = -> [Part012[Body007.Pocket013.Face25]]
  _Version = 2
FEATURE [PartDesign::SubShapeBinder] Binder018
  BindCopyOnChange = 0
  BindMode = 0
  ClaimChildren = false
  Context = -> Assembly [Part013.Body008.Binder018.]
  Fuse = false
  MakeFace = true
  OffsetFill = false
  OffsetIntersection = false
  OffsetJoinType = 0
  OffsetOpenResult = false
  PartialLoad = false
  Refine = true
  Relative = true
  Support = -> [Part011[Body006.Chamfer001.Face5]]
  _Version = 2
FEATURE [Sketcher::SketchObject] Sketch039
  ArcFitTolerance = 1e-06
  AttachmentSupport = -> [Binder017]
  ExternalGeometry = -> [Binder017,Binder018]
  FullyConstrained = true
  MakeInternals = false
  MapMode = 5
  Placement = pos=(0,0,25.4) rot=(0,0,1;0rad)
  sketch-geometry (4):
    g0: LineSegment StartX=53.4062 StartY=9 StartZ=0 EndX=87.3367 EndY=9 EndZ=0
    g1: LineSegment StartX=87.3367 StartY=9 StartZ=0 EndX=87.3367 EndY=20 EndZ=0
    g2: LineSegment StartX=87.3367 StartY=20 StartZ=0 EndX=53.4062 EndY=20 EndZ=0
    g3: LineSegment StartX=53.4062 StartY=20 StartZ=0 EndX=53.4062 EndY=9 EndZ=0
  constraints (12):
    c: Coincident(g0,g1)
    c: Coincident(g1,g2)
    c: Coincident(g2,g3)
    c: Coincident(g3,g0)
    c: Horizontal(g0)
    c: Horizontal(g2)
    c: Vertical(g1)
    c: Vertical(g3)
    c: Distance(g2,g-4) = 6
    c: Distance(g-4,g1) = 5
    c: Distance(g-4,g3) = 5
    c: PointOnObject(g0,g-3)
FEATURE [PartDesign::Pad] Pad014
  Direction = (0,0,1)
  Length = 48
  Length2 = 10
  Profile = -> Sketch039
  ReferenceAxis = -> Sketch039 [N_Axis]
  Refine = true
  Reversed = true
  Suppressed = false
  Type = 0
FEATURE [PartDesign::SubShapeBinder] Binder019
  BindCopyOnChange = 0
  BindMode = 0
  ClaimChildren = false
  Context = -> Assembly [Part013.Body008.Binder019.]
  Fuse = false
  MakeFace = true
  OffsetFill = false
  OffsetIntersection = false
  OffsetJoinType = 0
  OffsetOpenResult = false
  PartialLoad = false
  Refine = true
  Relative = true
  Support = -> [Part011[Body006.Chamfer001.Face4]]
  _Version = 2
FEATURE [Sketcher::SketchObject] Sketch040
  ArcFitTolerance = 1e-06
  AttachmentSupport = -> [Binder018]
  ExternalGeometry = -> [Binder018]
  FullyConstrained = true
  MakeInternals = false
  MapMode = 5
  Placement = pos=(0,0,-1.6) rot=(0,0,1;0rad)
  sketch-geometry (4):
    g0: LineSegment StartX=58.4062 StartY=14 StartZ=0 EndX=82.3367 EndY=14 EndZ=0
    g1: LineSegment StartX=82.3367 StartY=14 StartZ=0 EndX=79.45 EndY=9 EndZ=0
    g2: LineSegment StartX=79.45 StartY=9 StartZ=0 EndX=61.293 EndY=9 EndZ=0
    g3: LineSegment StartX=61.293 StartY=9 StartZ=0 EndX=58.4062 EndY=14 EndZ=0
  constraints (8):
    c: Coincident(g0,g-4)
    c: Coincident(g1,g0)
    c: Coincident(g1,g-5)
    c: Coincident(g2,g1)
    c: Coincident(g2,g-4)
    c: Coincident(g3,g2)
    c: Coincident(g3,g0)
    c: Coincident(g-5,g0)
FEATURE [Sketcher::SketchObject] Sketch041
  ArcFitTolerance = 1e-06
  AttachmentSupport = -> [Binder019]
  ExternalGeometry = -> [Binder019]
  FullyConstrained = true
  MakeInternals = false
  MapMode = 5
  Placement = pos=(0,0,-23.6) rot=(1,0,0;3.14159rad)
  sketch-geometry (4):
    g0: LineSegment StartX=56.2847 StartY=-14 StartZ=0 EndX=84.4582 EndY=-14 EndZ=0
    g1: LineSegment StartX=84.4582 StartY=-14 StartZ=0 EndX=81.5715 EndY=-9 EndZ=0
    g2: LineSegment StartX=81.5715 StartY=-9 StartZ=0 EndX=59.1715 EndY=-9 EndZ=0
    g3: LineSegment StartX=59.1715 StartY=-9 StartZ=0 EndX=56.2847 EndY=-14 EndZ=0
  constraints (8):
    c: Coincident(g0,g-5)
    c: Coincident(g0,g-4)
    c: Coincident(g1,g0)
    c: Coincident(g1,g-4)
    c: Coincident(g2,g1)
    c: Coincident(g2,g-5)
    c: Coincident(g3,g2)
    c: Coincident(g3,g0)
FEATURE [PartDesign::SubtractiveLoft] SubtractiveLoft
  BaseFeature = -> Pad014
  Closed = false
  Profile = -> Sketch041
  Refine = true
  Ruled = false
  Sections = -> [Sketch040]
  Suppressed = false
FEATURE [PartDesign::Pocket] Pocket014
  BaseFeature = -> SubtractiveLoft
  Direction = (0,0,1)
  Length = 15
  Length2 = 5
  Profile = -> SubtractiveLoft [Face6]
  Refine = true
  Suppressed = false
  Type = 0
FEATURE [PartDesign::Chamfer] Chamfer002
  Angle = 45
  Base = -> Pocket014 [Edge11,Edge14,Edge12,Edge13,Edge30,Edge16,Edge17,Edge15]
  BaseFeature = -> Pocket014
  ChamferType = 0
  FlipDirection = false
  Refine = true
  Size = 2
  Size2 = 1
  SupportTransform = false
  Suppressed = false
  UseAllEdges = false
FEATURE [PartDesign::Body] Body008
  AllowCompound = false
  Group = -> [Binder018,Binder017,Sketch039,Pad014,Binder019,Sketch040,Sketch041,SubtractiveLoft,Pocket014,Chamfer002]
  Origin = -> Origin024
  Tip = -> Chamfer002
FEATURE [App::Part] Part013  label="Enclosure Cap"
  Group = -> [Body008]
  Origin = -> Origin023
FEATURE [PartDesign::Chamfer] Chamfer003
  Angle = 45
  Base = -> Chamfer001 [Edge67,Edge20,Edge68,Edge21,Edge5,Edge16,Edge56]
  BaseFeature = -> Chamfer001
  ChamferType = 0
  FlipDirection = false
  Refine = true
  Size = 3
  Size2 = 1
  SupportTransform = false
  Suppressed = false
  UseAllEdges = false
FEATURE [PartDesign::Chamfer] Chamfer004
  Angle = 45
  Base = -> Chamfer003 [Edge1,Edge17]
  BaseFeature = -> Chamfer003
  ChamferType = 0
  FlipDirection = false
  Refine = true
  Size = 1
  Size2 = 1
  SupportTransform = false
  Suppressed = false
  UseAllEdges = false
FEATURE [PartDesign::Chamfer] Chamfer005
  Angle = 45
  Base = -> Chamfer004 [Edge5,Edge7,Edge9]
  BaseFeature = -> Chamfer004
  ChamferType = 0
  FlipDirection = false
  Refine = true
  Size = 1
  Size2 = 1
  SupportTransform = false
  Suppressed = false
  UseAllEdges = false
FEATURE [PartDesign::Body] Body006
  AllowCompound = false
  Group = -> [Binder008,Binder009,Binder010,Binder011,Sketch030,Pad009,Sketch031,Pad010,Sketch032,Pocket011,Sketch036,Hole,Sketch038,Pad013,Chamfer001,Chamfer003,Chamfer004,Chamfer005]
  Origin = -> Origin020
  Tip = -> Chamfer005
FEATURE [App::Part] Part011  label="Enclosure Back"
  Group = -> [Body006]
  Origin = -> Origin019
FEATURE [PartDesign::Chamfer] Chamfer006
  Angle = 45
  Base = -> Pocket013 [Edge43,Edge41,Edge54,Edge50,Edge51,Edge39,Edge47,Edge46]
  BaseFeature = -> Pocket013
  ChamferType = 0
  FlipDirection = false
  Refine = true
  Size = 3
  Size2 = 1
  SupportTransform = false
  Suppressed = false
  UseAllEdges = false
FEATURE [PartDesign::Body] Body007
  AllowCompound = false
  Group = -> [Binder012,Binder013,Binder014,Binder015,Sketch033,Pad011,Sketch034,Pad012,Sketch035,Pocket012,Chamfer,Binder016,Fillet,Sketch037,Pocket013,Chamfer006]
  Origin = -> Origin022
  Tip = -> Chamfer006
FEATURE [App::Part] Part012  label="Enclosure Front"
  Group = -> [Body007]
  Origin = -> Origin021
FEATURE [Assembly::AssemblyObject] Assembly  label="Ec"
  Group = -> [Joints,Board_bfa0,Part,Part006,Part007,Part008,GroundedJoint,Part009,Joint,Joint001,Joint002,Joint003,Joint004,Joint005,Joint006,Joint007,Joint008,Joint009,Joint010,Joint011,Joint012,Joint013,Part010,Joint014,Part011,Part012,Part013]
  Origin = -> Origin
  Type = Assembly
